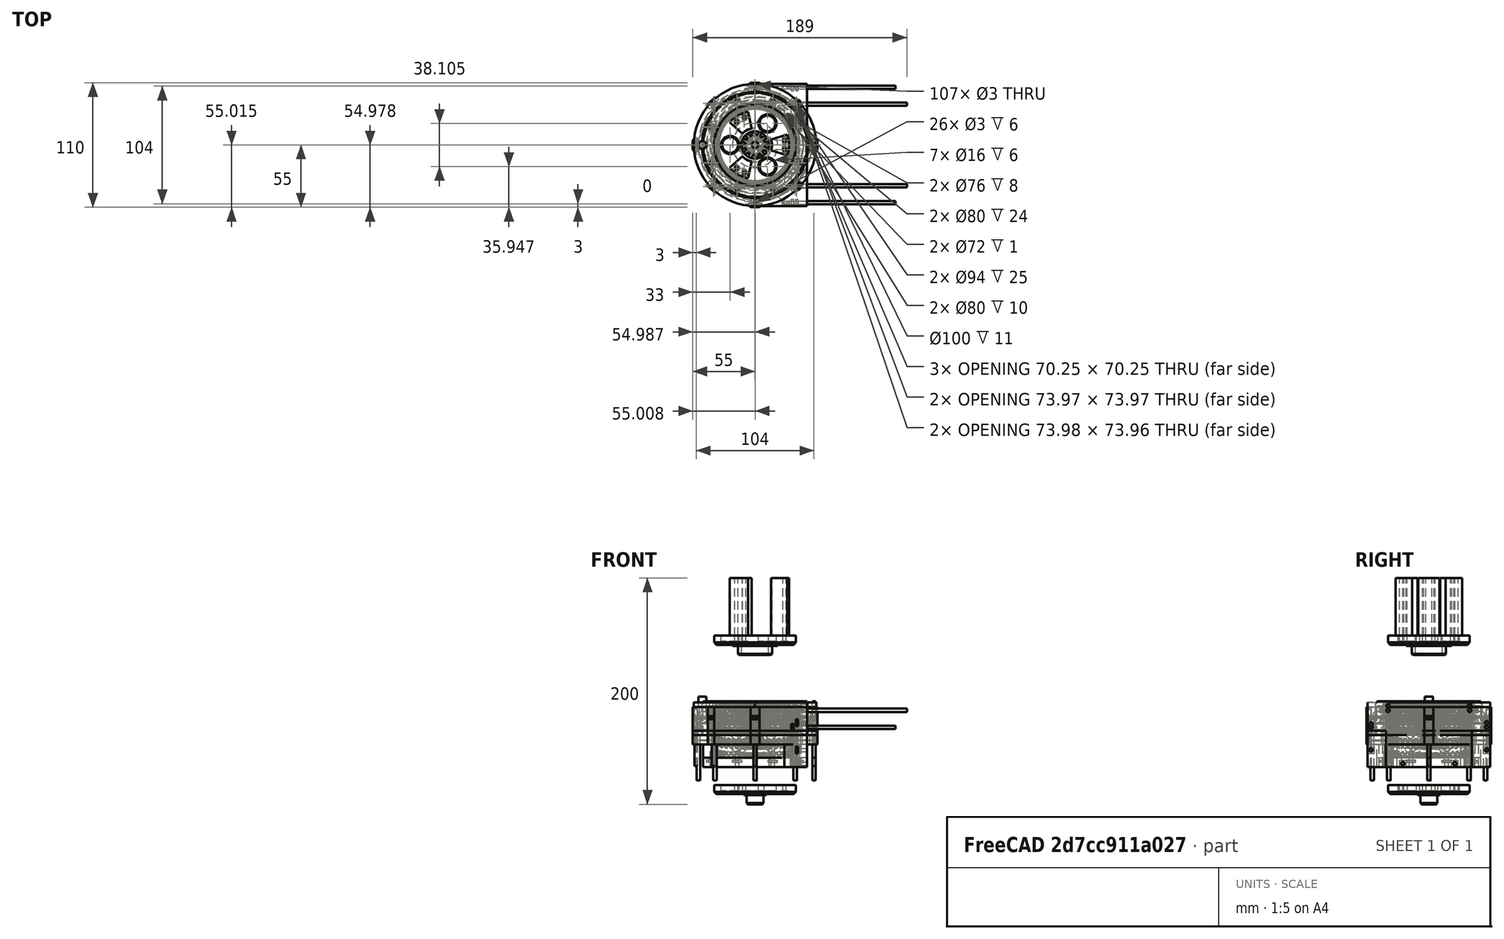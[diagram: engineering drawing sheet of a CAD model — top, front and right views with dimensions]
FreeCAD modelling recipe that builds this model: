
FCSTD DOCUMENT  (FreeCAD 0.19R24276 (Git))
Label: J-midi-deep-thin_039
License: All rights reserved
LicenseURL: http://en.wikipedia.org/wiki/All_rights_reserved
objects: Part::Cylinder×296, Part::Box×209, Part::Compound×127, Part::Cut×109, Part::FeaturePython×43, Part::Chamfer×31, Part::Torus×4, Part::Wedge×4, Mesh::Feature×3, Part::Mirroring×2, Part::Fillet×1
note: 826 computed .brp shape members not serialized (recipe doc carries the construction recipe); baked Part::Feature solids carry a one-line shape summary decoded from their .brp

FEATURE [Part::Torus] Torus004  label="Anuloid004"
  Angle1 = -180
  Angle2 = 180
  Angle3 = 360
  AttacherType = Attacher::AttachEngine3D
  Placement = pos=(0,0,34) rot=(0,0,1;0rad)
  Radius1 = 46.2
  Radius2 = 3.1
FEATURE [Part::Torus] Torus005  label="Anuloid005"
  Angle1 = -180
  Angle2 = 180
  Angle3 = 360
  AttacherType = Attacher::AttachEngine3D
  Placement = pos=(0,0,34) rot=(0,0,1;0rad)
  Radius1 = 46.2
  Radius2 = 3.1
FEATURE [Part::Box] Box157  label="Krychle157"
  AttacherType = Attacher::AttachEngine3D
  Height = 2
  Length = 8
  Placement = pos=(46,-3,23) rot=(0,0,1;0rad)
  Width = 6
FEATURE [Part::Cylinder] Cylinder006  label="Válec006"
  Angle = 360
  AttacherType = Attacher::AttachEngine3D
  Height = 16
  Placement = pos=(-45.6,0,34) rot=(0,0,1;0rad)
  Radius = 3.5
FEATURE [Part::Box] Box156  label="Krychle156"
  AttacherType = Attacher::AttachEngine3D
  Height = 25
  Length = 46
  Placement = pos=(0,-54,20) rot=(0,0,1;0rad)
  Width = 108
FEATURE [Part::Box] Box158  label="Krychle158"
  AttacherType = Attacher::AttachEngine3D
  Height = 2
  Length = 8
  Placement = pos=(34.6482,30.4056,23) rot=(0,0,1;0.785398rad)
  Width = 6
FEATURE [Part::Box] Box159  label="Krychle159"
  AttacherType = Attacher::AttachEngine3D
  Height = 2
  Length = 8
  Placement = pos=(3,46,23) rot=(0,0,1;1.5708rad)
  Width = 6
FEATURE [Part::Box] Box160  label="Krychle160"
  AttacherType = Attacher::AttachEngine3D
  Height = 2
  Length = 8
  Placement = pos=(-30.4056,34.6482,23) rot=(0,0,1;2.35619rad)
  Width = 6
FEATURE [Part::Box] Box161  label="Krychle161"
  AttacherType = Attacher::AttachEngine3D
  Height = 2
  Length = 8
  Placement = pos=(-46,3,23) rot=(0,0,1;3.14159rad)
  Width = 6
FEATURE [Part::Cylinder] Cylinder374  label="Válec374"
  Angle = 360
  AttacherType = Attacher::AttachEngine3D
  Height = 50
  Placement = pos=(50,0,-15) rot=(0,0,1;0rad)
  Radius = 1.5
FEATURE [Part::Cylinder] Cylinder375  label="Válec375"
  Angle = 360
  AttacherType = Attacher::AttachEngine3D
  Height = 50
  Placement = pos=(35.3553,35.3553,-15) rot=(0,0,1;0.785398rad)
  Radius = 1.5
FEATURE [Part::Cylinder] Cylinder376  label="Válec376"
  Angle = 360
  AttacherType = Attacher::AttachEngine3D
  Height = 50
  Placement = pos=(-7e-15,50,-15) rot=(0,0,1;1.5708rad)
  Radius = 1.5
FEATURE [Part::Box] Box162  label="Krychle162"
  AttacherType = Attacher::AttachEngine3D
  Height = 2
  Length = 8
  Placement = pos=(-34.6482,-30.4056,23) rot=(0,0,1;3.92699rad)
  Width = 6
FEATURE [Part::Box] Box163  label="Krychle163"
  AttacherType = Attacher::AttachEngine3D
  Height = 2
  Length = 8
  Placement = pos=(-3,-46,23) rot=(0,0,-1;1.5708rad)
  Width = 6
FEATURE [Part::Box] Box164  label="Krychle164"
  AttacherType = Attacher::AttachEngine3D
  Height = 2
  Length = 8
  Placement = pos=(30.4056,-34.6482,23) rot=(0,0,-1;0.785398rad)
  Width = 6
FEATURE [Part::Compound] Compound297
  Links = -> [Box157,Box158,Box159,Box160,Box161,Box162,Box163,Box164]
  Placement = pos=(0,0,1) rot=(0,0,1;0rad)
FEATURE [Part::Cylinder] Cylinder377  label="Válec377"
  Angle = 360
  AttacherType = Attacher::AttachEngine3D
  Height = 50
  Placement = pos=(-35.3553,35.3553,-15) rot=(0,0,1;2.35619rad)
  Radius = 1.5
FEATURE [Part::Cylinder] Cylinder378  label="Válec378"
  Angle = 360
  AttacherType = Attacher::AttachEngine3D
  Height = 50
  Placement = pos=(-50,-2.3e-14,-15) rot=(0,0,1;3.14159rad)
  Radius = 1.5
FEATURE [Part::Cylinder] Cylinder379  label="Válec379"
  Angle = 360
  AttacherType = Attacher::AttachEngine3D
  Height = 50
  Placement = pos=(-35.3553,-35.3553,-15) rot=(0,0,1;3.92699rad)
  Radius = 1.5
FEATURE [Part::Cylinder] Cylinder380  label="Válec380"
  Angle = 360
  AttacherType = Attacher::AttachEngine3D
  Height = 50
  Placement = pos=(2.5e-14,-50,-15) rot=(0,0,-1;1.5708rad)
  Radius = 1.5
FEATURE [Part::Cylinder] Cylinder381  label="Válec381"
  Angle = 360
  AttacherType = Attacher::AttachEngine3D
  Height = 50
  Placement = pos=(35.3553,-35.3553,-15) rot=(0,0,-1;0.785398rad)
  Radius = 1.5
FEATURE [Part::Compound] Compound298
  Links = -> [Cylinder374,Cylinder375,Cylinder376,Cylinder377,Cylinder378,Cylinder379,Cylinder380,Cylinder381]
  Placement = pos=(0,0,-5) rot=(0,0,1;0rad)
FEATURE [Part::Box] Box165  label="Krychle165"
  AttacherType = Attacher::AttachEngine3D
  Height = 2
  Length = 8
  Placement = pos=(3,46,23) rot=(0,0,1;1.5708rad)
  Width = 6
FEATURE [Part::Box] Box166  label="Krychle166"
  AttacherType = Attacher::AttachEngine3D
  Height = 2
  Length = 8
  Placement = pos=(-30.4056,34.6482,23) rot=(0,0,1;2.35619rad)
  Width = 6
FEATURE [Part::Box] Box167  label="Krychle167"
  AttacherType = Attacher::AttachEngine3D
  Height = 2
  Length = 8
  Placement = pos=(46,-3,23) rot=(0,0,1;0rad)
  Width = 6
FEATURE [Part::Box] Box168  label="Krychle168"
  AttacherType = Attacher::AttachEngine3D
  Height = 2
  Length = 8
  Placement = pos=(-46,3,23) rot=(0,0,1;3.14159rad)
  Width = 6
FEATURE [Part::Box] Box169  label="Krychle169"
  AttacherType = Attacher::AttachEngine3D
  Height = 2
  Length = 8
  Placement = pos=(-34.6482,-30.4056,23) rot=(0,0,1;3.92699rad)
  Width = 6
FEATURE [Part::Box] Box170  label="Krychle170"
  AttacherType = Attacher::AttachEngine3D
  Height = 2
  Length = 8
  Placement = pos=(30.4056,-34.6482,23) rot=(0,0,-1;0.785398rad)
  Width = 6
FEATURE [Part::Box] Box171  label="Krychle171"
  AttacherType = Attacher::AttachEngine3D
  Height = 2
  Length = 8
  Placement = pos=(34.6482,30.4056,23) rot=(0,0,1;0.785398rad)
  Width = 6
FEATURE [Part::Box] Box172  label="Krychle172"
  AttacherType = Attacher::AttachEngine3D
  Height = 2
  Length = 8
  Placement = pos=(-3,-46,23) rot=(0,0,-1;1.5708rad)
  Width = 6
FEATURE [Part::Compound] Compound300
  Links = -> [Box167,Box171,Box165,Box166,Box168,Box169,Box172,Box170]
  Placement = pos=(0,0,1) rot=(0,0,1;0rad)
FEATURE [Part::Cylinder] Cylinder  label="Válec"
  Angle = 360
  AttacherType = Attacher::AttachEngine3D
  Height = 25
  Placement = pos=(0,0,20) rot=(0,0,1;0rad)
  Radius = 47
FEATURE [Part::Cut] Cut153
  Base = -> Box156
  Tool = -> Cylinder
FEATURE [Part::Cut] Cut154
  Base = -> Cut153
  Tool = -> Torus005
FEATURE [Part::Cut] Cut155
  Base = -> Cut154
  Tool = -> Compound298
FEATURE [Part::Box] Box173  label="Krychle173"
  AttacherType = Attacher::AttachEngine3D
  Height = 6
  Length = 2
  Placement = pos=(32,48,24) rot=(0,0,1;0rad)
  Width = 6
FEATURE [Part::Cylinder] Cylinder391  label="Válec391"
  Angle = 360
  AttacherType = Attacher::AttachEngine3D
  Height = 100
  Placement = pos=(24,51,27) rot=(0,1,0;1.5708rad)
  Radius = 1.5
FEATURE [Part::Cylinder] Cylinder392  label="Válec392"
  Angle = 360
  AttacherType = Attacher::AttachEngine3D
  Height = 100
  Placement = pos=(24,-51,26) rot=(0,1,0;1.5708rad)
  Radius = 1.5
FEATURE [Part::Box] Box174  label="Krychle174"
  AttacherType = Attacher::AttachEngine3D
  Height = 6
  Length = 2
  Placement = pos=(32,-54,24) rot=(0,0,1;0rad)
  Width = 6
FEATURE [Part::Box] Box175  label="Krychle175"
  AttacherType = Attacher::AttachEngine3D
  Height = 6
  Length = 2
  Placement = pos=(38,33,39) rot=(0,0,1;0rad)
  Width = 6
FEATURE [Part::Cylinder] Cylinder393  label="Válec393"
  Angle = 360
  AttacherType = Attacher::AttachEngine3D
  Height = 100
  Placement = pos=(34,36,42) rot=(0,1,0;1.5708rad)
  Radius = 1.5
FEATURE [Part::Cylinder] Cylinder394  label="Válec394"
  Angle = 360
  AttacherType = Attacher::AttachEngine3D
  Height = 100
  Placement = pos=(34,-36,42) rot=(0,1,0;1.5708rad)
  Radius = 1.5
FEATURE [Part::Compound] Compound301
  Links = -> [Cylinder391,Cylinder392,Cylinder393,Cylinder394]
FEATURE [Part::Box] Box176  label="Krychle176"
  AttacherType = Attacher::AttachEngine3D
  Height = 6
  Length = 2
  Placement = pos=(38,-39,39) rot=(0,0,1;0rad)
  Width = 6
FEATURE [Part::Compound] Compound302
  Links = -> [Box173,Box174,Box175,Box176]
FEATURE [Part::Cylinder] Cylinder395  label="Válec395"
  Angle = 360
  AttacherType = Attacher::AttachEngine3D
  Height = 100
  Placement = pos=(34,-36,42) rot=(0,1,0;1.5708rad)
  Radius = 1.5
FEATURE [Part::Cylinder] Cylinder396  label="Válec396"
  Angle = 360
  AttacherType = Attacher::AttachEngine3D
  Height = 100
  Placement = pos=(24,51,27) rot=(0,1,0;1.5708rad)
  Radius = 1.5
FEATURE [Part::Cylinder] Cylinder397  label="Válec397"
  Angle = 360
  AttacherType = Attacher::AttachEngine3D
  Height = 100
  Placement = pos=(24,-51,27) rot=(0,1,0;1.5708rad)
  Radius = 1.5
FEATURE [Part::Cylinder] Cylinder398  label="Válec398"
  Angle = 360
  AttacherType = Attacher::AttachEngine3D
  Height = 100
  Placement = pos=(34,36,42) rot=(0,1,0;1.5708rad)
  Radius = 1.5
FEATURE [Part::Compound] Compound303
  Links = -> [Cylinder396,Cylinder397,Cylinder398,Cylinder395]
FEATURE [Part::Box] Box177  label="Krychle177"
  AttacherType = Attacher::AttachEngine3D
  Height = 6
  Length = 2
  Placement = pos=(36,48,24) rot=(0,0,1;0rad)
  Width = 6
FEATURE [Part::Box] Box178  label="Krychle178"
  AttacherType = Attacher::AttachEngine3D
  Height = 6
  Length = 2
  Placement = pos=(36,-54,24) rot=(0,0,1;0rad)
  Width = 6
FEATURE [Part::Box] Box179  label="Krychle179"
  AttacherType = Attacher::AttachEngine3D
  Height = 6
  Length = 2
  Placement = pos=(38,33,39) rot=(0,0,1;0rad)
  Width = 6
FEATURE [Part::Box] Box180  label="Krychle180"
  AttacherType = Attacher::AttachEngine3D
  Height = 6
  Length = 2
  Placement = pos=(38,-39,39) rot=(0,0,1;0rad)
  Width = 6
FEATURE [Part::Compound] Compound304
  Links = -> [Box177,Box178,Box179,Box180]
FEATURE [Part::FeaturePython] Tube002  # WARN: FeaturePython — macro-defined, semantics opaque (R4)
  AttacherType = Attacher::AttachEngine3D
  Height = 25
  InnerRadius = 47
  OuterRadius = 54
  Placement = pos=(0,0,20) rot=(0,0,1;0rad)
FEATURE [Part::Cut] Cut156
  Base = -> Cut155
  Tool = -> Compound300
FEATURE [Part::Cut] Cut157
  Base = -> Cut156
  Tool = -> Compound301
FEATURE [Part::Cut] Cut158
  Base = -> Cut157
  Tool = -> Compound304
FEATURE [Part::Cut] Cut009
  Base = -> Tube002
  Tool = -> Torus004
FEATURE [Part::Cut] Cut010
  Base = -> Cut009
  Tool = -> Cylinder006
FEATURE [Part::Cut] Cut151
  Base = -> Cut010
  Tool = -> Compound297
FEATURE [Part::Cut] Cut152
  Base = -> Cut151
  Tool = -> Compound298
FEATURE [Part::Cut] Cut159
  Base = -> Cut152
  Tool = -> Compound303
FEATURE [Part::Cut] Cut160
  Base = -> Cut159
  Tool = -> Compound302
FEATURE [Part::Compound] Compound728  label="J-midi-deep_bearing-ring"
  Links = -> [Cut160,Cut158]
  Placement = pos=(0,0,4) rot=(0,0,1;0rad)
FEATURE [Part::Torus] Torus009  label="Anuloid009"
  Angle1 = -180
  Angle2 = 180
  Angle3 = 360
  AttacherType = Attacher::AttachEngine3D
  Placement = pos=(0,0,34) rot=(0,0,1;0rad)
  Radius1 = 46
  Radius2 = 3.1
FEATURE [Part::Box] Box424  label="Krychle424"
  AttacherType = Attacher::AttachEngine3D
  Height = 2
  Length = 6
  Placement = pos=(30.4056,-34.6482,33) rot=(0,0,1;0.785398rad)
  Width = 8
FEATURE [Part::Cylinder] Cylinder1114  label="Válec1114"
  Angle = 360
  AttacherType = Attacher::AttachEngine3D
  Height = 20
  Placement = pos=(-46.4,0,34) rot=(0,0,1;0rad)
  Radius = 3.5
FEATURE [Part::Box] Box425  label="Krychle425"
  AttacherType = Attacher::AttachEngine3D
  Height = 2
  Length = 6
  Placement = pos=(3,46,33) rot=(0,0,1;3.14159rad)
  Width = 8
FEATURE [Part::Box] Box426  label="Krychle426"
  AttacherType = Attacher::AttachEngine3D
  Height = 2
  Length = 6
  Placement = pos=(-3,-46,33) rot=(0,0,1;0rad)
  Width = 8
FEATURE [Part::Cylinder] Cylinder1115  label="Válec1115"
  Angle = 360
  AttacherType = Attacher::AttachEngine3D
  Height = 12
  Radius = 40
FEATURE [Part::Cylinder] Cylinder1116  label="Válec1116"
  Angle = 360
  AttacherType = Attacher::AttachEngine3D
  Height = 12
  Radius = 40
FEATURE [Part::Box] Box427  label="Krychle427"
  AttacherType = Attacher::AttachEngine3D
  Height = 2
  Length = 6
  Placement = pos=(-46,3,33) rot=(0,0,-1;1.5708rad)
  Width = 8
FEATURE [Part::Box] Box428  label="Krychle428"
  AttacherType = Attacher::AttachEngine3D
  Height = 2
  Length = 6
  Placement = pos=(-3,-46,33) rot=(0,0,1;0rad)
  Width = 8
FEATURE [Part::Box] Box429  label="Krychle429"
  AttacherType = Attacher::AttachEngine3D
  Height = 2
  Length = 6
  Placement = pos=(-46,3,33) rot=(0,0,-1;1.5708rad)
  Width = 8
FEATURE [Part::Box] Box430  label="Krychle430"
  AttacherType = Attacher::AttachEngine3D
  Height = 2
  Length = 6
  Placement = pos=(-34.6482,-30.4056,33) rot=(0,0,-1;0.785398rad)
  Width = 8
FEATURE [Part::Box] Box431  label="Krychle431"
  AttacherType = Attacher::AttachEngine3D
  Height = 2
  Length = 6
  Placement = pos=(46,-3,33) rot=(0,0,1;1.5708rad)
  Width = 8
FEATURE [Part::Box] Box432  label="Krychle432"
  AttacherType = Attacher::AttachEngine3D
  Height = 2
  Length = 6
  Placement = pos=(34.6482,30.4056,33) rot=(0,0,1;2.35619rad)
  Width = 8
FEATURE [Part::Box] Box433  label="Krychle433"
  AttacherType = Attacher::AttachEngine3D
  Height = 2
  Length = 6
  Placement = pos=(30.4056,-34.6482,33) rot=(0,0,1;0.785398rad)
  Width = 8
FEATURE [Part::Box] Box434  label="Krychle434"
  AttacherType = Attacher::AttachEngine3D
  Height = 2
  Length = 6
  Placement = pos=(-30.4056,34.6482,33) rot=(0,0,1;3.92699rad)
  Width = 8
FEATURE [Part::Compound] Compound870
  Links = -> [Box430,Box424,Box431,Box428,Box432,Box425,Box434,Box427]
  Placement = pos=(0,0,7) rot=(0,0,1;0.392699rad)
FEATURE [Part::Box] Box435  label="Krychle435"
  AttacherType = Attacher::AttachEngine3D
  Height = 2
  Length = 6
  Placement = pos=(46,-3,33) rot=(0,0,1;1.5708rad)
  Width = 8
FEATURE [Part::Box] Box436  label="Krychle436"
  AttacherType = Attacher::AttachEngine3D
  Height = 2
  Length = 6
  Placement = pos=(3,46,33) rot=(0,0,1;3.14159rad)
  Width = 8
FEATURE [Part::Cylinder] Cylinder1117  label="Válec1117"
  Angle = 360
  AttacherType = Attacher::AttachEngine3D
  Height = 20
  Placement = pos=(-46.4,0,34) rot=(0,0,1;0rad)
  Radius = 3.5
FEATURE [Part::Cylinder] Cylinder1118  label="Válec1118"
  Angle = 360
  AttacherType = Attacher::AttachEngine3D
  Height = 32
  Placement = pos=(-29.6985,-29.6985,33.5) rot=(0,0,-1;0.785398rad)
  Radius = 1.5
FEATURE [Part::Cylinder] Cylinder1119  label="Válec1119"
  Angle = 360
  AttacherType = Attacher::AttachEngine3D
  Height = 12
  Placement = pos=(-29.6985,-29.6985,33.5) rot=(0,0,-1;0.785398rad)
  Radius = 1.5
FEATURE [Part::Cylinder] Cylinder1120  label="Válec1120"
  Angle = 360
  AttacherType = Attacher::AttachEngine3D
  Height = 12
  Placement = pos=(29.6985,-29.6985,33.5) rot=(0,0,1;0.785398rad)
  Radius = 1.5
FEATURE [Part::Box] Box437  label="Krychle437"
  AttacherType = Attacher::AttachEngine3D
  Height = 2
  Length = 6
  Placement = pos=(-34.6482,-30.4056,33) rot=(0,0,-1;0.785398rad)
  Width = 8
FEATURE [Part::Cylinder] Cylinder1121  label="Válec1121"
  Angle = 360
  AttacherType = Attacher::AttachEngine3D
  Height = 32
  Placement = pos=(0,-42,33.5) rot=(0,0,1;0rad)
  Radius = 1.5
FEATURE [Part::Cylinder] Cylinder1122  label="Válec1122"
  Angle = 360
  AttacherType = Attacher::AttachEngine3D
  Height = 12
  Placement = pos=(0,-42,33.5) rot=(0,0,1;0rad)
  Radius = 1.5
FEATURE [Part::Cylinder] Cylinder1123  label="Válec1123"
  Angle = 360
  AttacherType = Attacher::AttachEngine3D
  Height = 32
  Placement = pos=(-1.4e-14,42,33.5) rot=(0,0,1;3.14159rad)
  Radius = 1.5
FEATURE [Part::Cylinder] Cylinder1124  label="Válec1124"
  Angle = 360
  AttacherType = Attacher::AttachEngine3D
  Height = 12
  Placement = pos=(-42,-2.4e-14,33.5) rot=(0,0,-1;1.5708rad)
  Radius = 1.5
FEATURE [Part::Cylinder] Cylinder1125  label="Válec1125"
  Angle = 360
  AttacherType = Attacher::AttachEngine3D
  Height = 12
  Placement = pos=(-1.4e-14,42,33.5) rot=(0,0,1;3.14159rad)
  Radius = 1.5
FEATURE [Part::Box] Box438  label="Krychle438"
  AttacherType = Attacher::AttachEngine3D
  Height = 2
  Length = 6
  Placement = pos=(34.6482,30.4056,33) rot=(0,0,1;2.35619rad)
  Width = 8
FEATURE [Part::Cylinder] Cylinder1126  label="Válec1126"
  Angle = 360
  AttacherType = Attacher::AttachEngine3D
  Height = 12
  Placement = pos=(29.6985,29.6985,33.5) rot=(0,0,1;2.35619rad)
  Radius = 1.5
FEATURE [Part::Box] Box439  label="Krychle439"
  AttacherType = Attacher::AttachEngine3D
  Height = 2
  Length = 6
  Placement = pos=(-34.6482,-30.4056,33) rot=(0,0,-1;0.785398rad)
  Width = 8
FEATURE [Part::Box] Box440  label="Krychle440"
  AttacherType = Attacher::AttachEngine3D
  Height = 2
  Length = 6
  Placement = pos=(-30.4056,34.6482,33) rot=(0,0,1;3.92699rad)
  Width = 8
FEATURE [Part::Compound] Compound873
  Links = -> [Box439,Box433,Box435,Box426,Box438,Box436,Box440,Box429]
  Placement = pos=(0,0,7) rot=(0,0,1;0.392699rad)
FEATURE [Part::Cylinder] Cylinder1127  label="Válec1127"
  Angle = 360
  AttacherType = Attacher::AttachEngine3D
  Height = 12
  Placement = pos=(-29.6985,29.6985,33.5) rot=(0,0,1;3.92699rad)
  Radius = 1.5
FEATURE [Part::Cylinder] Cylinder1128  label="Válec1128"
  Angle = 360
  AttacherType = Attacher::AttachEngine3D
  Height = 12
  Placement = pos=(42,6e-15,33.5) rot=(0,0,1;1.5708rad)
  Radius = 1.5
FEATURE [Part::Compound] Compound874
  Links = -> [Cylinder1122,Cylinder1120,Cylinder1128,Cylinder1126,Cylinder1125,Cylinder1127,Cylinder1124,Cylinder1119]
  Placement = pos=(0,0,4) rot=(0,0,1;0.392699rad)
FEATURE [Part::Box] Box441  label="Krychle441"
  AttacherType = Attacher::AttachEngine3D
  Height = 2
  Length = 6
  Placement = pos=(-30.4056,34.6482,33) rot=(0,0,1;3.92699rad)
  Width = 8
FEATURE [Part::Box] Box442  label="Krychle442"
  AttacherType = Attacher::AttachEngine3D
  Height = 2
  Length = 6
  Placement = pos=(-3,-46,33) rot=(0,0,1;0rad)
  Width = 8
FEATURE [Part::Box] Box443  label="Krychle443"
  AttacherType = Attacher::AttachEngine3D
  Height = 2
  Length = 6
  Placement = pos=(46,-3,33) rot=(0,0,1;1.5708rad)
  Width = 8
FEATURE [Part::Cylinder] Cylinder1129  label="Válec1129"
  Angle = 360
  AttacherType = Attacher::AttachEngine3D
  Height = 32
  Placement = pos=(-29.6985,29.6985,33.5) rot=(0,0,1;3.92699rad)
  Radius = 1.5
FEATURE [Part::Box] Box444  label="Krychle444"
  AttacherType = Attacher::AttachEngine3D
  Height = 2
  Length = 6
  Placement = pos=(-46,3,33) rot=(0,0,-1;1.5708rad)
  Width = 8
FEATURE [Part::Box] Box445  label="Krychle445"
  AttacherType = Attacher::AttachEngine3D
  Height = 2
  Length = 6
  Placement = pos=(30.4056,-34.6482,33) rot=(0,0,1;0.785398rad)
  Width = 8
FEATURE [Part::Cylinder] Cylinder1130  label="Válec1130"
  Angle = 360
  AttacherType = Attacher::AttachEngine3D
  Height = 32
  Placement = pos=(-42,-2.4e-14,33.5) rot=(0,0,-1;1.5708rad)
  Radius = 1.5
FEATURE [Part::Box] Box446  label="Krychle446"
  AttacherType = Attacher::AttachEngine3D
  Height = 2
  Length = 6
  Placement = pos=(3,46,33) rot=(0,0,1;3.14159rad)
  Width = 8
FEATURE [Part::Cylinder] Cylinder1131  label="Válec1131"
  Angle = 360
  AttacherType = Attacher::AttachEngine3D
  Height = 32
  Placement = pos=(29.6985,29.6985,33.5) rot=(0,0,1;2.35619rad)
  Radius = 1.5
FEATURE [Part::Box] Box447  label="Krychle447"
  AttacherType = Attacher::AttachEngine3D
  Height = 2
  Length = 6
  Placement = pos=(34.6482,30.4056,33) rot=(0,0,1;2.35619rad)
  Width = 8
FEATURE [Part::Compound] Compound869
  Links = -> [Box437,Box445,Box443,Box442,Box447,Box446,Box441,Box444]
  Placement = pos=(0,0,7) rot=(0,0,1;0.392699rad)
FEATURE [Part::Cylinder] Cylinder1132  label="Válec1132"
  Angle = 360
  AttacherType = Attacher::AttachEngine3D
  Height = 32
  Placement = pos=(42,6e-15,33.5) rot=(0,0,1;1.5708rad)
  Radius = 1.5
FEATURE [Part::Cylinder] Cylinder1133  label="Válec1133"
  Angle = 360
  AttacherType = Attacher::AttachEngine3D
  Height = 32
  Placement = pos=(29.6985,-29.6985,33.5) rot=(0,0,1;0.785398rad)
  Radius = 1.5
FEATURE [Part::Compound] Compound871
  Links = -> [Cylinder1121,Cylinder1133,Cylinder1132,Cylinder1131,Cylinder1123,Cylinder1129,Cylinder1130,Cylinder1118]
  Placement = pos=(0,0,4) rot=(0,0,1;0.392699rad)
FEATURE [Part::FeaturePython] wormgear065  # WARN: FeaturePython — macro-defined, semantics opaque (R4)
  AttacherType = Attacher::AttachEngine3D
  Placement = pos=(0,0,0) rot=(0,0,-1;0.1309rad)
  beta = 38.7636
  clearance = 0.25
  diameter = 67.25
  head = 0
  height = 14
  module = 1.5
  pressure_angle = 20
  reverse_pitch = false
  teeth = 36
  version = 0.0.3
FEATURE [Part::Cut] Cut418
  Base = -> Cylinder1116
  Placement = pos=(0,0,21) rot=(0,0,1;0.258309rad)
  Tool = -> wormgear065
FEATURE [Part::FeaturePython] Tube100  # WARN: FeaturePython — macro-defined, semantics opaque (R4)
  AttacherType = Attacher::AttachEngine3D
  Height = 24
  InnerRadius = 40
  OuterRadius = 46
  Placement = pos=(0,0,21) rot=(0,0,1;0rad)
FEATURE [Part::Cut] Cut419
  Base = -> Tube100
  Tool = -> Torus009
FEATURE [Part::Cut] Cut426
  Base = -> Cut419
  Tool = -> Cylinder1114
FEATURE [Part::Cut] Cut420
  Base = -> Cut426
  Tool = -> Compound871
FEATURE [Part::Cut] Cut421
  Base = -> Cut420
  Tool = -> Compound869
FEATURE [Part::FeaturePython] wormgear066  # WARN: FeaturePython — macro-defined, semantics opaque (R4)
  AttacherType = Attacher::AttachEngine3D
  Placement = pos=(0,0,0) rot=(0,0,1;0.10472rad)
  beta = 38.7636
  clearance = 0.25
  diameter = 67.25
  head = 0
  height = 14
  module = 1.5
  pressure_angle = 20
  reverse_pitch = true
  teeth = 36
  version = 0.0.3
FEATURE [Part::Cut] Cut423
  Base = -> Cylinder1115
  Placement = pos=(0,0,33) rot=(0,0,1;0.466876rad)
  Tool = -> wormgear066
FEATURE [Part::Cut] Cut427
  Base = -> Cut423
  Tool = -> Compound870
FEATURE [Part::Compound] Compound872
  Links = -> [Cut427,Cut418]
FEATURE [Part::FeaturePython] Tube101  # WARN: FeaturePython — macro-defined, semantics opaque (R4)
  AttacherType = Attacher::AttachEngine3D
  Height = 1
  InnerRadius = 36
  OuterRadius = 46
  Placement = pos=(0,0,45) rot=(0,0,1;0rad)
FEATURE [Part::Cut] Cut424
  Base = -> Tube101
  Tool = -> Cylinder1117
FEATURE [Part::Cut] Cut425
  Base = -> Cut424
  Tool = -> Compound874
FEATURE [Part::Cut] Cut422
  Base = -> Cut425
  Tool = -> Compound873
FEATURE [Part::Compound] Compound875  label="J-midi_actuator-ring-m1.5_v4"
  Links = -> [Cut421,Cut422,Compound872]
FEATURE [Part::FeaturePython] Tube102  # WARN: FeaturePython — macro-defined, semantics opaque (R4)
  AttacherType = Attacher::AttachEngine3D
  Height = 25
  InnerRadius = 47
  OuterRadius = 54
  Placement = pos=(0,0,20) rot=(0,0,1;0rad)
FEATURE [Part::FeaturePython] Tube103  # WARN: FeaturePython — macro-defined, semantics opaque (R4)
  AttacherType = Attacher::AttachEngine3D
  Height = 24
  InnerRadius = 40
  OuterRadius = 46
  Placement = pos=(0,0,21) rot=(0,0,1;0rad)
FEATURE [Part::FeaturePython] Tube  label="61816"  # WARN: FeaturePython — macro-defined, semantics opaque (R4)
  AttacherType = Attacher::AttachEngine3D
  Height = 10
  InnerRadius = 40
  OuterRadius = 50
  Placement = pos=(0,0,20) rot=(0,0,1;0rad)
FEATURE [Part::Cylinder] Cylinder1134  label="Válec1134"
  Angle = 360
  AttacherType = Attacher::AttachEngine3D
  Height = 50
  Placement = pos=(52,0,-15) rot=(0,0,1;0rad)
  Radius = 1.5
FEATURE [Part::Cylinder] Cylinder1135  label="Válec1135"
  Angle = 360
  AttacherType = Attacher::AttachEngine3D
  Height = 50
  Placement = pos=(35.3553,35.3553,-15) rot=(0,0,1;0.785398rad)
  Radius = 1.5
FEATURE [Part::Cylinder] Cylinder1136  label="Válec1136"
  Angle = 360
  AttacherType = Attacher::AttachEngine3D
  Height = 50
  Placement = pos=(-7e-15,50,-15) rot=(0,0,1;1.5708rad)
  Radius = 1.5
FEATURE [Part::Cylinder] Cylinder1137  label="Válec1137"
  Angle = 360
  AttacherType = Attacher::AttachEngine3D
  Height = 50
  Placement = pos=(-35.3553,35.3553,-15) rot=(0,0,1;2.35619rad)
  Radius = 1.5
FEATURE [Part::Cylinder] Cylinder1138  label="Válec1138"
  Angle = 360
  AttacherType = Attacher::AttachEngine3D
  Height = 50
  Placement = pos=(-50,-2.3e-14,-15) rot=(0,0,1;3.14159rad)
  Radius = 1.5
FEATURE [Part::Cylinder] Cylinder1139  label="Válec1139"
  Angle = 360
  AttacherType = Attacher::AttachEngine3D
  Height = 50
  Placement = pos=(-35.3553,-35.3553,-15) rot=(0,0,1;3.92699rad)
  Radius = 1.5
FEATURE [Part::Cylinder] Cylinder1140  label="Válec1140"
  Angle = 360
  AttacherType = Attacher::AttachEngine3D
  Height = 50
  Placement = pos=(2.5e-14,-50,-15) rot=(0,0,-1;1.5708rad)
  Radius = 1.5
FEATURE [Part::Cylinder] Cylinder1141  label="Válec1141"
  Angle = 360
  AttacherType = Attacher::AttachEngine3D
  Height = 50
  Placement = pos=(35.3553,-35.3553,-15) rot=(0,0,-1;0.785398rad)
  Radius = 1.5
FEATURE [Part::Compound] Compound876
  Links = -> [Cylinder1134,Cylinder1135,Cylinder1136,Cylinder1137,Cylinder1138,Cylinder1139,Cylinder1140,Cylinder1141]
  Placement = pos=(0,0,-5) rot=(0,0,1;0rad)
FEATURE [Part::Cylinder] Cylinder1142  label="Válec1142"
  Angle = 360
  AttacherType = Attacher::AttachEngine3D
  Height = 50
  Placement = pos=(52,0,0) rot=(0,0,1;0rad)
  Radius = 1.5
FEATURE [Part::Cut] Cut  label="Thino"
  Base = -> Tube102
  Tool = -> Cylinder1142
FEATURE [Part::Box] Box448  label="Krychle448"
  AttacherType = Attacher::AttachEngine3D
  Height = 2
  Length = 8
  Placement = pos=(3,46,23) rot=(0,0,1;1.5708rad)
  Width = 6
FEATURE [Part::Box] Box449  label="Krychle449"
  AttacherType = Attacher::AttachEngine3D
  Height = 2
  Length = 8
  Placement = pos=(-30.4056,34.6482,23) rot=(0,0,1;2.35619rad)
  Width = 6
FEATURE [Part::Box] Box450  label="Krychle450"
  AttacherType = Attacher::AttachEngine3D
  Height = 2
  Length = 8
  Placement = pos=(46,-3,23) rot=(0,0,1;0rad)
  Width = 6
FEATURE [Part::Box] Box451  label="Krychle451"
  AttacherType = Attacher::AttachEngine3D
  Height = 2
  Length = 8
  Placement = pos=(-46,3,23) rot=(0,0,1;3.14159rad)
  Width = 6
FEATURE [Part::Box] Box452  label="Krychle452"
  AttacherType = Attacher::AttachEngine3D
  Height = 2
  Length = 8
  Placement = pos=(-34.6482,-30.4056,23) rot=(0,0,1;3.92699rad)
  Width = 6
FEATURE [Part::Box] Box453  label="Krychle453"
  AttacherType = Attacher::AttachEngine3D
  Height = 2
  Length = 8
  Placement = pos=(30.4056,-34.6482,23) rot=(0,0,-1;0.785398rad)
  Width = 6
FEATURE [Part::Box] Box454  label="Krychle454"
  AttacherType = Attacher::AttachEngine3D
  Height = 2
  Length = 8
  Placement = pos=(34.6482,30.4056,23) rot=(0,0,1;0.785398rad)
  Width = 6
FEATURE [Part::Box] Box455  label="Krychle455"
  AttacherType = Attacher::AttachEngine3D
  Height = 2
  Length = 8
  Placement = pos=(-3,-46,23) rot=(0,0,-1;1.5708rad)
  Width = 6
FEATURE [Part::Compound] Compound877
  Links = -> [Box450,Box454,Box448,Box449,Box451,Box452,Box455,Box453]
  Placement = pos=(0,0,1) rot=(0,0,1;0rad)
FEATURE [Part::Box] Box456  label="Krychle456"
  AttacherType = Attacher::AttachEngine3D
  Height = 2
  Length = 8
  Placement = pos=(47,-3,34) rot=(0,0,1;0rad)
  Width = 6
FEATURE [Part::FeaturePython] Tube104  # WARN: FeaturePython — macro-defined, semantics opaque (R4)
  AttacherType = Attacher::AttachEngine3D
  Height = 25
  InnerRadius = 47
  OuterRadius = 54
  Placement = pos=(0,0,20) rot=(0,0,1;0rad)
FEATURE [Part::Cylinder] Cylinder1143  label="Válec1143"
  Angle = 360
  AttacherType = Attacher::AttachEngine3D
  Height = 50
  Placement = pos=(52,0,0) rot=(0,0,1;0rad)
  Radius = 1.5
FEATURE [Part::Box] Box457  label="Krychle457"
  AttacherType = Attacher::AttachEngine3D
  Height = 25
  Length = 4
  Placement = pos=(51,-6,20) rot=(0,0,1;0rad)
  Width = 12
FEATURE [Part::Chamfer] Chamfer
  Base = -> Box457
  Edges = 2 edges r=2: [Edge5,Edge7]
FEATURE [Part::Cylinder] Cylinder1144  label="Válec1144"
  Angle = 360
  AttacherType = Attacher::AttachEngine3D
  Height = 50
  Placement = pos=(52,0,0) rot=(0,0,1;0rad)
  Radius = 1.5
FEATURE [Part::Cylinder] Cylinder1145  label="Válec1145"
  Angle = 360
  AttacherType = Attacher::AttachEngine3D
  Height = 50
  Placement = pos=(52,0,0) rot=(0,0,1;0rad)
  Radius = 1.5
FEATURE [Part::Cut] Cut428
  Base = -> Chamfer
  Tool = -> Cylinder1144
FEATURE [Part::Compound] Compound  label="J-midi_thin-ring_old"
  Links = -> [Cut,Cut428]
FEATURE [Part::FeaturePython] Tube105  label="ZKL-61816"  # WARN: FeaturePython — macro-defined, semantics opaque (R4)
  AttacherType = Attacher::AttachEngine3D
  Height = 10
  InnerRadius = 40
  OuterRadius = 50
  Placement = pos=(0,0,20) rot=(0,0,1;0rad)
FEATURE [Part::FeaturePython] Tube106  label="ZKL-61816-2"  # WARN: FeaturePython — macro-defined, semantics opaque (R4)
  AttacherType = Attacher::AttachEngine3D
  Height = 10
  InnerRadius = 40
  OuterRadius = 50
  Placement = pos=(0,0,20) rot=(0,0,1;0rad)
FEATURE [Part::FeaturePython] Tube107  # WARN: FeaturePython — macro-defined, semantics opaque (R4)
  AttacherType = Attacher::AttachEngine3D
  Height = 25
  InnerRadius = 47
  OuterRadius = 54
  Placement = pos=(0,0,20) rot=(0,0,1;0rad)
FEATURE [Part::Box] Box458  label="Krychle458"
  AttacherType = Attacher::AttachEngine3D
  Height = 25
  Length = 4
  Placement = pos=(51,-6,20) rot=(0,0,1;0rad)
  Width = 12
FEATURE [Part::Chamfer] Chamfer001
  Base = -> Box458
  Edges = 2 edges r=2: [Edge5,Edge7]
FEATURE [Part::Chamfer] Chamfer002
  Base = -> Box458
  Edges = 2 edges r=2: [Edge5,Edge7]
  Placement = pos=(0,0,0) rot=(0,0,1;0.785398rad)
FEATURE [Part::Chamfer] Chamfer003
  Base = -> Box458
  Edges = 2 edges r=2: [Edge5,Edge7]
  Placement = pos=(0,0,0) rot=(0,0,1;1.5708rad)
FEATURE [Part::Chamfer] Chamfer004
  Base = -> Box458
  Edges = 2 edges r=2: [Edge5,Edge7]
  Placement = pos=(0,0,0) rot=(0,0,1;2.35619rad)
FEATURE [Part::FeaturePython] Tube108  label="ZKL-61816-3"  # WARN: FeaturePython — macro-defined, semantics opaque (R4)
  AttacherType = Attacher::AttachEngine3D
  Height = 10
  InnerRadius = 40
  OuterRadius = 50
  Placement = pos=(0,0,25) rot=(0,0,1;0rad)
FEATURE [Part::FeaturePython] Tube109  label="ZKL-61816-003"  # WARN: FeaturePython — macro-defined, semantics opaque (R4)
  AttacherType = Attacher::AttachEngine3D
  Height = 11
  InnerRadius = 40
  OuterRadius = 50
  Placement = pos=(0,0,20) rot=(0,0,1;0rad)
FEATURE [Part::Chamfer] Chamfer005
  Base = -> Box458
  Edges = 2 edges r=2: [Edge5,Edge7]
  Placement = pos=(0,0,0) rot=(0,0,1;3.14159rad)
FEATURE [Part::Chamfer] Chamfer006
  Base = -> Box458
  Edges = 2 edges r=2: [Edge5,Edge7]
  Placement = pos=(0,0,0) rot=(0,0,1;3.92699rad)
FEATURE [Part::Chamfer] Chamfer007
  Base = -> Box458
  Edges = 2 edges r=2: [Edge5,Edge7]
  Placement = pos=(0,0,0) rot=(0,0,-1;1.5708rad)
FEATURE [Part::Chamfer] Chamfer008
  Base = -> Box458
  Edges = 2 edges r=2: [Edge5,Edge7]
  Placement = pos=(0,0,0) rot=(0,0,-1;0.785398rad)
FEATURE [Part::Compound] Compound878
  Links = -> [Chamfer001,Chamfer002,Chamfer003,Chamfer004,Chamfer005,Chamfer006,Chamfer007,Chamfer008]
FEATURE [Part::Cut] Cut429
  Base = -> Tube107
  Tool = -> Tube109
FEATURE [Part::Cylinder] Cylinder1152  label="Válec1152"
  Angle = 360
  AttacherType = Attacher::AttachEngine3D
  Height = 50
  Placement = pos=(52,0,0) rot=(0,0,1;0rad)
  Radius = 1.5
FEATURE [Part::Cylinder] Cylinder1153  label="Válec1153"
  Angle = 360
  AttacherType = Attacher::AttachEngine3D
  Height = 50
  Placement = pos=(36.7696,36.7696,0) rot=(0,0,1;0.785398rad)
  Radius = 1.5
FEATURE [Part::Cylinder] Cylinder1154  label="Válec1154"
  Angle = 360
  AttacherType = Attacher::AttachEngine3D
  Height = 50
  Placement = pos=(-7e-15,52,0) rot=(0,0,1;1.5708rad)
  Radius = 1.5
FEATURE [Part::Cylinder] Cylinder1155  label="Válec1155"
  Angle = 360
  AttacherType = Attacher::AttachEngine3D
  Height = 50
  Placement = pos=(-36.7696,36.7696,0) rot=(0,0,1;2.35619rad)
  Radius = 1.5
FEATURE [Part::Cylinder] Cylinder1156  label="Válec1156"
  Angle = 360
  AttacherType = Attacher::AttachEngine3D
  Height = 50
  Placement = pos=(-52,-2.1e-14,0) rot=(0,0,1;3.14159rad)
  Radius = 1.5
FEATURE [Part::Cylinder] Cylinder1157  label="Válec1157"
  Angle = 360
  AttacherType = Attacher::AttachEngine3D
  Height = 50
  Placement = pos=(-36.7696,-36.7696,0) rot=(0,0,1;3.92699rad)
  Radius = 1.5
FEATURE [Part::Cylinder] Cylinder1158  label="Válec1158"
  Angle = 360
  AttacherType = Attacher::AttachEngine3D
  Height = 50
  Placement = pos=(2e-14,-52,0) rot=(0,0,-1;1.5708rad)
  Radius = 1.5
FEATURE [Part::Cylinder] Cylinder1159  label="Válec1159"
  Angle = 360
  AttacherType = Attacher::AttachEngine3D
  Height = 50
  Placement = pos=(36.7696,-36.7696,0) rot=(0,0,-1;0.785398rad)
  Radius = 1.5
FEATURE [Part::Cylinder] Cylinder1160  label="Válec1160"
  Angle = 360
  AttacherType = Attacher::AttachEngine3D
  Height = 50
  Placement = pos=(52,0,0) rot=(0,0,1;0rad)
  Radius = 1.5
FEATURE [Part::Cylinder] Cylinder1161  label="Válec1161"
  Angle = 360
  AttacherType = Attacher::AttachEngine3D
  Height = 50
  Placement = pos=(36.7696,36.7696,0) rot=(0,0,1;0.785398rad)
  Radius = 1.5
FEATURE [Part::Cylinder] Cylinder1162  label="Válec1162"
  Angle = 360
  AttacherType = Attacher::AttachEngine3D
  Height = 50
  Placement = pos=(-7e-15,52,0) rot=(0,0,1;1.5708rad)
  Radius = 1.5
FEATURE [Part::Cylinder] Cylinder1163  label="Válec1163"
  Angle = 360
  AttacherType = Attacher::AttachEngine3D
  Height = 50
  Placement = pos=(-36.7696,36.7696,0) rot=(0,0,1;2.35619rad)
  Radius = 1.5
FEATURE [Part::Compound] Compound880
  Links = -> [Cylinder1152,Cylinder1153,Cylinder1154,Cylinder1155,Cylinder1156,Cylinder1157,Cylinder1158,Cylinder1159]
  Placement = pos=(0,0,-7) rot=(0,0,1;0rad)
FEATURE [Part::Cut] Cut430
  Base = -> Compound878
  Tool = -> Compound880
FEATURE [Part::Cylinder] Cylinder1164  label="Válec1164"
  Angle = 360
  AttacherType = Attacher::AttachEngine3D
  Height = 50
  Placement = pos=(-52,-2.1e-14,0) rot=(0,0,1;3.14159rad)
  Radius = 1.5
FEATURE [Part::Cylinder] Cylinder1165  label="Válec1165"
  Angle = 360
  AttacherType = Attacher::AttachEngine3D
  Height = 50
  Placement = pos=(-36.7696,-36.7696,0) rot=(0,0,1;3.92699rad)
  Radius = 1.5
FEATURE [Part::Cylinder] Cylinder1166  label="Válec1166"
  Angle = 360
  AttacherType = Attacher::AttachEngine3D
  Height = 50
  Placement = pos=(2e-14,-52,0) rot=(0,0,-1;1.5708rad)
  Radius = 1.5
FEATURE [Part::Cylinder] Cylinder1167  label="Válec1167"
  Angle = 360
  AttacherType = Attacher::AttachEngine3D
  Height = 50
  Placement = pos=(36.7696,-36.7696,0) rot=(0,0,-1;0.785398rad)
  Radius = 1.5
FEATURE [Part::Compound] Compound879
  Links = -> [Cylinder1160,Cylinder1161,Cylinder1162,Cylinder1163,Cylinder1164,Cylinder1165,Cylinder1166,Cylinder1167]
  Placement = pos=(0,0,-7) rot=(0,0,1;0rad)
FEATURE [Part::Cut] Cut431
  Base = -> Cut429
  Tool = -> Compound879
FEATURE [Part::Box] Box459  label="Krychle459"
  AttacherType = Attacher::AttachEngine3D
  Height = 2
  Length = 8
  Placement = pos=(47,-3,34) rot=(0,0,1;0rad)
  Width = 6
FEATURE [Part::Box] Box460  label="Krychle460"
  AttacherType = Attacher::AttachEngine3D
  Height = 2
  Length = 8
  Placement = pos=(35.3553,31.1127,34) rot=(0,0,1;0.785398rad)
  Width = 6
FEATURE [Part::Box] Box461  label="Krychle461"
  AttacherType = Attacher::AttachEngine3D
  Height = 2
  Length = 8
  Placement = pos=(3,47,34) rot=(0,0,1;1.5708rad)
  Width = 6
FEATURE [Part::Box] Box462  label="Krychle462"
  AttacherType = Attacher::AttachEngine3D
  Height = 2
  Length = 8
  Placement = pos=(-31.1127,35.3553,34) rot=(0,0,1;2.35619rad)
  Width = 6
FEATURE [Part::Box] Box463  label="Krychle463"
  AttacherType = Attacher::AttachEngine3D
  Height = 2
  Length = 8
  Placement = pos=(-47,3,34) rot=(0,0,1;3.14159rad)
  Width = 6
FEATURE [Part::Box] Box464  label="Krychle464"
  AttacherType = Attacher::AttachEngine3D
  Height = 2
  Length = 8
  Placement = pos=(-35.3553,-31.1127,34) rot=(0,0,1;3.92699rad)
  Width = 6
FEATURE [Part::Box] Box465  label="Krychle465"
  AttacherType = Attacher::AttachEngine3D
  Height = 2
  Length = 8
  Placement = pos=(-3,-47,34) rot=(0,0,-1;1.5708rad)
  Width = 6
FEATURE [Part::Box] Box466  label="Krychle466"
  AttacherType = Attacher::AttachEngine3D
  Height = 2
  Length = 8
  Placement = pos=(31.1127,-35.3553,34) rot=(0,0,-1;0.785398rad)
  Width = 6
FEATURE [Part::Compound] Compound881
  Links = -> [Box459,Box460,Box461,Box462,Box463,Box464,Box465,Box466]
  Placement = pos=(0,0,1) rot=(0,0,1;0rad)
FEATURE [Part::Box] Box467  label="Krychle467"
  AttacherType = Attacher::AttachEngine3D
  Height = 2
  Length = 8
  Placement = pos=(47,-3,34) rot=(0,0,1;0rad)
  Width = 6
FEATURE [Part::Box] Box468  label="Krychle468"
  AttacherType = Attacher::AttachEngine3D
  Height = 2
  Length = 8
  Placement = pos=(35.3553,31.1127,34) rot=(0,0,1;0.785398rad)
  Width = 6
FEATURE [Part::Box] Box469  label="Krychle469"
  AttacherType = Attacher::AttachEngine3D
  Height = 2
  Length = 8
  Placement = pos=(3,47,34) rot=(0,0,1;1.5708rad)
  Width = 6
FEATURE [Part::Box] Box470  label="Krychle470"
  AttacherType = Attacher::AttachEngine3D
  Height = 2
  Length = 8
  Placement = pos=(-31.1127,35.3553,34) rot=(0,0,1;2.35619rad)
  Width = 6
FEATURE [Part::Box] Box471  label="Krychle471"
  AttacherType = Attacher::AttachEngine3D
  Height = 2
  Length = 8
  Placement = pos=(-47,3,34) rot=(0,0,1;3.14159rad)
  Width = 6
FEATURE [Part::Box] Box472  label="Krychle472"
  AttacherType = Attacher::AttachEngine3D
  Height = 2
  Length = 8
  Placement = pos=(-35.3553,-31.1127,34) rot=(0,0,1;3.92699rad)
  Width = 6
FEATURE [Part::Box] Box473  label="Krychle473"
  AttacherType = Attacher::AttachEngine3D
  Height = 2
  Length = 8
  Placement = pos=(-3,-47,34) rot=(0,0,-1;1.5708rad)
  Width = 6
FEATURE [Part::Box] Box474  label="Krychle474"
  AttacherType = Attacher::AttachEngine3D
  Height = 2
  Length = 8
  Placement = pos=(31.1127,-35.3553,34) rot=(0,0,-1;0.785398rad)
  Width = 6
FEATURE [Part::Compound] Compound882
  Links = -> [Box467,Box468,Box469,Box470,Box471,Box472,Box473,Box474]
  Placement = pos=(0,0,1) rot=(0,0,1;0rad)
FEATURE [Part::Cut] Cut432
  Base = -> Cut431
  Tool = -> Compound881
FEATURE [Part::Cut] Cut433
  Base = -> Cut430
  Tool = -> Compound882
FEATURE [Part::Box] Box475  label="Krychle475"
  AttacherType = Attacher::AttachEngine3D
  Height = 6
  Length = 2
  Placement = pos=(32,48,24) rot=(0,0,1;0rad)
  Width = 6
FEATURE [Part::Box] Box476  label="Krychle476"
  AttacherType = Attacher::AttachEngine3D
  Height = 6
  Length = 2
  Placement = pos=(32,-54,24) rot=(0,0,1;0rad)
  Width = 6
FEATURE [Part::Box] Box477  label="Krychle477"
  AttacherType = Attacher::AttachEngine3D
  Height = 6
  Length = 2
  Placement = pos=(38,33,39) rot=(0,0,1;0rad)
  Width = 6
FEATURE [Part::Box] Box478  label="Krychle478"
  AttacherType = Attacher::AttachEngine3D
  Height = 6
  Length = 2
  Placement = pos=(38,-39,39) rot=(0,0,1;0rad)
  Width = 6
FEATURE [Part::Compound] Compound884
  Links = -> [Box475,Box476,Box477,Box478]
FEATURE [Part::Cylinder] Cylinder1168  label="Válec1168"
  Angle = 360
  AttacherType = Attacher::AttachEngine3D
  Height = 100
  Placement = pos=(34,-36,42) rot=(0,1,0;1.5708rad)
  Radius = 1.5
FEATURE [Part::Cylinder] Cylinder1169  label="Válec1169"
  Angle = 360
  AttacherType = Attacher::AttachEngine3D
  Height = 100
  Placement = pos=(24,51,27) rot=(0,1,0;1.5708rad)
  Radius = 1.5
FEATURE [Part::Cylinder] Cylinder1170  label="Válec1170"
  Angle = 360
  AttacherType = Attacher::AttachEngine3D
  Height = 100
  Placement = pos=(24,-51,27) rot=(0,1,0;1.5708rad)
  Radius = 1.5
FEATURE [Part::Cylinder] Cylinder1171  label="Válec1171"
  Angle = 360
  AttacherType = Attacher::AttachEngine3D
  Height = 100
  Placement = pos=(34,36,42) rot=(0,1,0;1.5708rad)
  Radius = 1.5
FEATURE [Part::Compound] Compound883
  Links = -> [Cylinder1169,Cylinder1170,Cylinder1171,Cylinder1168]
FEATURE [Part::Box] Box479  label="Krychle479"
  AttacherType = Attacher::AttachEngine3D
  Height = 25
  Length = 46
  Placement = pos=(0,-54,20) rot=(0,0,1;0rad)
  Width = 108
FEATURE [Part::Cylinder] Cylinder1172  label="Válec1172"
  Angle = 360
  AttacherType = Attacher::AttachEngine3D
  Height = 25
  Placement = pos=(0,0,20) rot=(0,0,1;0rad)
  Radius = 47
FEATURE [Part::Cut] Cut434
  Base = -> Box479
  Tool = -> Cylinder1172
FEATURE [Part::Box] Box480  label="Krychle480"
  AttacherType = Attacher::AttachEngine3D
  Height = 25
  Length = 46
  Placement = pos=(0,-54,20) rot=(0,0,1;0rad)
  Width = 108
FEATURE [Part::Cylinder] Cylinder1173  label="Válec1173"
  Angle = 360
  AttacherType = Attacher::AttachEngine3D
  Height = 25
  Placement = pos=(0,0,20) rot=(0,0,1;0rad)
  Radius = 47
FEATURE [Part::Cut] Cut435
  Base = -> Box480
  Tool = -> Cylinder1173
FEATURE [Part::FeaturePython] Tube110  label="ZKL-61816-4"  # WARN: FeaturePython — macro-defined, semantics opaque (R4)
  AttacherType = Attacher::AttachEngine3D
  Height = 10
  InnerRadius = 40
  OuterRadius = 50
  Placement = pos=(0,0,20) rot=(0,0,1;0rad)
FEATURE [Part::Cut] Cut436
  Base = -> Cut435
  Tool = -> Tube110
FEATURE [Part::Box] Box481  label="Krychle481"
  AttacherType = Attacher::AttachEngine3D
  Height = 25
  Length = 46
  Placement = pos=(0,-54,20) rot=(0,0,1;0rad)
  Width = 108
FEATURE [Part::Cylinder] Cylinder1174  label="Válec1174"
  Angle = 360
  AttacherType = Attacher::AttachEngine3D
  Height = 25
  Placement = pos=(0,0,20) rot=(0,0,1;0rad)
  Radius = 47
FEATURE [Part::Cut] Cut437
  Base = -> Box481
  Tool = -> Cylinder1174
FEATURE [Part::FeaturePython] Tube111  label="ZKL-61816-004"  # WARN: FeaturePython — macro-defined, semantics opaque (R4)
  AttacherType = Attacher::AttachEngine3D
  Height = 11
  InnerRadius = 40
  OuterRadius = 50
  Placement = pos=(0,0,20) rot=(0,0,1;0rad)
FEATURE [Part::Cut] Cut438
  Base = -> Cut437
  Tool = -> Tube111
FEATURE [Part::Cylinder] Cylinder1175  label="Válec1175"
  Angle = 360
  AttacherType = Attacher::AttachEngine3D
  Height = 50
  Placement = pos=(52,0,0) rot=(0,0,1;0rad)
  Radius = 1.5
FEATURE [Part::Cylinder] Cylinder1176  label="Válec1176"
  Angle = 360
  AttacherType = Attacher::AttachEngine3D
  Height = 50
  Placement = pos=(36.7696,36.7696,0) rot=(0,0,1;0.785398rad)
  Radius = 1.5
FEATURE [Part::Cylinder] Cylinder1177  label="Válec1177"
  Angle = 360
  AttacherType = Attacher::AttachEngine3D
  Height = 50
  Placement = pos=(-7e-15,52,0) rot=(0,0,1;1.5708rad)
  Radius = 1.5
FEATURE [Part::Cylinder] Cylinder1178  label="Válec1178"
  Angle = 360
  AttacherType = Attacher::AttachEngine3D
  Height = 50
  Placement = pos=(-36.7696,36.7696,0) rot=(0,0,1;2.35619rad)
  Radius = 1.5
FEATURE [Part::Cylinder] Cylinder1179  label="Válec1179"
  Angle = 360
  AttacherType = Attacher::AttachEngine3D
  Height = 50
  Placement = pos=(-52,-2.1e-14,0) rot=(0,0,1;3.14159rad)
  Radius = 1.5
FEATURE [Part::Cylinder] Cylinder1180  label="Válec1180"
  Angle = 360
  AttacherType = Attacher::AttachEngine3D
  Height = 50
  Placement = pos=(-36.7696,-36.7696,0) rot=(0,0,1;3.92699rad)
  Radius = 1.5
FEATURE [Part::Cylinder] Cylinder1181  label="Válec1181"
  Angle = 360
  AttacherType = Attacher::AttachEngine3D
  Height = 50
  Placement = pos=(2e-14,-52,0) rot=(0,0,-1;1.5708rad)
  Radius = 1.5
FEATURE [Part::Cylinder] Cylinder1182  label="Válec1182"
  Angle = 360
  AttacherType = Attacher::AttachEngine3D
  Height = 50
  Placement = pos=(36.7696,-36.7696,0) rot=(0,0,-1;0.785398rad)
  Radius = 1.5
FEATURE [Part::Compound] Compound885
  Links = -> [Cylinder1175,Cylinder1176,Cylinder1177,Cylinder1178,Cylinder1179,Cylinder1180,Cylinder1181,Cylinder1182]
  Placement = pos=(0,0,-7) rot=(0,0,1;0rad)
FEATURE [Part::Cut] Cut439
  Base = -> Cut438
  Tool = -> Compound885
FEATURE [Part::Box] Box482  label="Krychle482"
  AttacherType = Attacher::AttachEngine3D
  Height = 6
  Length = 2
  Placement = pos=(32,48,24) rot=(0,0,1;0rad)
  Width = 6
FEATURE [Part::Box] Box483  label="Krychle483"
  AttacherType = Attacher::AttachEngine3D
  Height = 6
  Length = 2
  Placement = pos=(32,-54,24) rot=(0,0,1;0rad)
  Width = 6
FEATURE [Part::Box] Box484  label="Krychle484"
  AttacherType = Attacher::AttachEngine3D
  Height = 6
  Length = 2
  Placement = pos=(38,33,39) rot=(0,0,1;0rad)
  Width = 6
FEATURE [Part::Box] Box485  label="Krychle485"
  AttacherType = Attacher::AttachEngine3D
  Height = 6
  Length = 2
  Placement = pos=(38,-39,39) rot=(0,0,1;0rad)
  Width = 6
FEATURE [Part::Compound] Compound886
  Links = -> [Box482,Box483,Box484,Box485]
FEATURE [Part::Cut] Cut440
  Base = -> Cut439
  Tool = -> Compound886
FEATURE [Part::Box] Box486  label="Krychle486"
  AttacherType = Attacher::AttachEngine3D
  Height = 6
  Length = 2
  Placement = pos=(32,48,24) rot=(0,0,1;0rad)
  Width = 6
FEATURE [Part::Box] Box487  label="Krychle487"
  AttacherType = Attacher::AttachEngine3D
  Height = 6
  Length = 2
  Placement = pos=(32,-54,24) rot=(0,0,1;0rad)
  Width = 6
FEATURE [Part::Box] Box488  label="Krychle488"
  AttacherType = Attacher::AttachEngine3D
  Height = 6
  Length = 2
  Placement = pos=(38,33,39) rot=(0,0,1;0rad)
  Width = 6
FEATURE [Part::Box] Box489  label="Krychle489"
  AttacherType = Attacher::AttachEngine3D
  Height = 6
  Length = 2
  Placement = pos=(38,-39,39) rot=(0,0,1;0rad)
  Width = 6
FEATURE [Part::Compound] Compound887
  Links = -> [Box486,Box487,Box488,Box489]
FEATURE [Part::Cut] Cut441
  Base = -> Cut433
  Tool = -> Compound887
FEATURE [Part::Box] Box490  label="Krychle490"
  AttacherType = Attacher::AttachEngine3D
  Height = 6
  Length = 2
  Placement = pos=(32,48,24) rot=(0,0,1;0rad)
  Width = 6
FEATURE [Part::Box] Box491  label="Krychle491"
  AttacherType = Attacher::AttachEngine3D
  Height = 6
  Length = 2
  Placement = pos=(32,-54,24) rot=(0,0,1;0rad)
  Width = 6
FEATURE [Part::Box] Box492  label="Krychle492"
  AttacherType = Attacher::AttachEngine3D
  Height = 6
  Length = 2
  Placement = pos=(38,33,39) rot=(0,0,1;0rad)
  Width = 6
FEATURE [Part::Box] Box493  label="Krychle493"
  AttacherType = Attacher::AttachEngine3D
  Height = 6
  Length = 2
  Placement = pos=(38,-39,39) rot=(0,0,1;0rad)
  Width = 6
FEATURE [Part::Compound] Compound888
  Links = -> [Box490,Box491,Box492,Box493]
FEATURE [Part::Cut] Cut442
  Base = -> Cut432
  Tool = -> Compound888
FEATURE [Part::Cylinder] Cylinder1183  label="Válec1183"
  Angle = 360
  AttacherType = Attacher::AttachEngine3D
  Height = 100
  Placement = pos=(34,-36,42) rot=(0,1,0;1.5708rad)
  Radius = 1.5
FEATURE [Part::Cylinder] Cylinder1184  label="Válec1184"
  Angle = 360
  AttacherType = Attacher::AttachEngine3D
  Height = 100
  Placement = pos=(24,51,27) rot=(0,1,0;1.5708rad)
  Radius = 1.5
FEATURE [Part::Cylinder] Cylinder1185  label="Válec1185"
  Angle = 360
  AttacherType = Attacher::AttachEngine3D
  Height = 100
  Placement = pos=(24,-51,27) rot=(0,1,0;1.5708rad)
  Radius = 1.5
FEATURE [Part::Cylinder] Cylinder1186  label="Válec1186"
  Angle = 360
  AttacherType = Attacher::AttachEngine3D
  Height = 100
  Placement = pos=(34,36,42) rot=(0,1,0;1.5708rad)
  Radius = 1.5
FEATURE [Part::Compound] Compound889
  Links = -> [Cylinder1184,Cylinder1185,Cylinder1186,Cylinder1183]
FEATURE [Part::Cylinder] Cylinder1187  label="Válec1187"
  Angle = 360
  AttacherType = Attacher::AttachEngine3D
  Height = 100
  Placement = pos=(34,-36,42) rot=(0,1,0;1.5708rad)
  Radius = 1.5
FEATURE [Part::Cylinder] Cylinder1188  label="Válec1188"
  Angle = 360
  AttacherType = Attacher::AttachEngine3D
  Height = 100
  Placement = pos=(24,51,27) rot=(0,1,0;1.5708rad)
  Radius = 1.5
FEATURE [Part::Cylinder] Cylinder1189  label="Válec1189"
  Angle = 360
  AttacherType = Attacher::AttachEngine3D
  Height = 100
  Placement = pos=(24,-51,27) rot=(0,1,0;1.5708rad)
  Radius = 1.5
FEATURE [Part::Cylinder] Cylinder1190  label="Válec1190"
  Angle = 360
  AttacherType = Attacher::AttachEngine3D
  Height = 100
  Placement = pos=(34,36,42) rot=(0,1,0;1.5708rad)
  Radius = 1.5
FEATURE [Part::Compound] Compound890
  Links = -> [Cylinder1188,Cylinder1189,Cylinder1190,Cylinder1187]
FEATURE [Part::Cut] Cut443
  Base = -> Cut440
  Tool = -> Compound889
FEATURE [Part::Cylinder] Cylinder1191  label="Válec1191"
  Angle = 360
  AttacherType = Attacher::AttachEngine3D
  Height = 100
  Placement = pos=(34,-36,42) rot=(0,1,0;1.5708rad)
  Radius = 1.5
FEATURE [Part::Cylinder] Cylinder1192  label="Válec1192"
  Angle = 360
  AttacherType = Attacher::AttachEngine3D
  Height = 100
  Placement = pos=(24,51,27) rot=(0,1,0;1.5708rad)
  Radius = 1.5
FEATURE [Part::Cylinder] Cylinder1193  label="Válec1193"
  Angle = 360
  AttacherType = Attacher::AttachEngine3D
  Height = 100
  Placement = pos=(24,-51,27) rot=(0,1,0;1.5708rad)
  Radius = 1.5
FEATURE [Part::Cylinder] Cylinder1194  label="Válec1194"
  Angle = 360
  AttacherType = Attacher::AttachEngine3D
  Height = 100
  Placement = pos=(34,36,42) rot=(0,1,0;1.5708rad)
  Radius = 1.5
FEATURE [Part::Compound] Compound891
  Links = -> [Cylinder1192,Cylinder1193,Cylinder1194,Cylinder1191]
FEATURE [Part::Cut] Cut444
  Base = -> Cut442
  Tool = -> Compound890
FEATURE [Part::Cut] Cut445
  Base = -> Cut441
  Tool = -> Compound891
FEATURE [Part::Cylinder] Cylinder1195  label="Válec1195"
  Angle = 360
  AttacherType = Attacher::AttachEngine3D
  Height = 50
  Placement = pos=(52,0,0) rot=(0,0,1;0rad)
  Radius = 1.5
FEATURE [Part::Cylinder] Cylinder1196  label="Válec1196"
  Angle = 360
  AttacherType = Attacher::AttachEngine3D
  Height = 50
  Placement = pos=(36.7696,36.7696,0) rot=(0,0,1;0.785398rad)
  Radius = 1.5
FEATURE [Part::Cylinder] Cylinder1197  label="Válec1197"
  Angle = 360
  AttacherType = Attacher::AttachEngine3D
  Height = 50
  Placement = pos=(-7e-15,52,0) rot=(0,0,1;1.5708rad)
  Radius = 1.5
FEATURE [Part::Cylinder] Cylinder1198  label="Válec1198"
  Angle = 360
  AttacherType = Attacher::AttachEngine3D
  Height = 50
  Placement = pos=(-36.7696,36.7696,0) rot=(0,0,1;2.35619rad)
  Radius = 1.5
FEATURE [Part::Cylinder] Cylinder1199  label="Válec1199"
  Angle = 360
  AttacherType = Attacher::AttachEngine3D
  Height = 50
  Placement = pos=(-52,-2.1e-14,0) rot=(0,0,1;3.14159rad)
  Radius = 1.5
FEATURE [Part::Cylinder] Cylinder1200  label="Válec1200"
  Angle = 360
  AttacherType = Attacher::AttachEngine3D
  Height = 50
  Placement = pos=(-36.7696,-36.7696,0) rot=(0,0,1;3.92699rad)
  Radius = 1.5
FEATURE [Part::Cylinder] Cylinder1201  label="Válec1201"
  Angle = 360
  AttacherType = Attacher::AttachEngine3D
  Height = 50
  Placement = pos=(2e-14,-52,0) rot=(0,0,-1;1.5708rad)
  Radius = 1.5
FEATURE [Part::Cylinder] Cylinder1202  label="Válec1202"
  Angle = 360
  AttacherType = Attacher::AttachEngine3D
  Height = 50
  Placement = pos=(36.7696,-36.7696,0) rot=(0,0,-1;0.785398rad)
  Radius = 1.5
FEATURE [Part::Compound] Compound892
  Links = -> [Cylinder1195,Cylinder1196,Cylinder1197,Cylinder1198,Cylinder1199,Cylinder1200,Cylinder1201,Cylinder1202]
  Placement = pos=(0,0,-7) rot=(0,0,1;0rad)
FEATURE [Part::Cylinder] Cylinder1203  label="Válec1203"
  Angle = 360
  AttacherType = Attacher::AttachEngine3D
  Height = 50
  Placement = pos=(52,0,0) rot=(0,0,1;0rad)
  Radius = 1.5
FEATURE [Part::Cylinder] Cylinder1204  label="Válec1204"
  Angle = 360
  AttacherType = Attacher::AttachEngine3D
  Height = 50
  Placement = pos=(36.7696,36.7696,0) rot=(0,0,1;0.785398rad)
  Radius = 1.5
FEATURE [Part::Cylinder] Cylinder1205  label="Válec1205"
  Angle = 360
  AttacherType = Attacher::AttachEngine3D
  Height = 50
  Placement = pos=(-7e-15,52,0) rot=(0,0,1;1.5708rad)
  Radius = 1.5
FEATURE [Part::Cylinder] Cylinder1206  label="Válec1206"
  Angle = 360
  AttacherType = Attacher::AttachEngine3D
  Height = 50
  Placement = pos=(-36.7696,36.7696,0) rot=(0,0,1;2.35619rad)
  Radius = 1.5
FEATURE [Part::Cylinder] Cylinder1207  label="Válec1207"
  Angle = 360
  AttacherType = Attacher::AttachEngine3D
  Height = 50
  Placement = pos=(-52,-2.1e-14,0) rot=(0,0,1;3.14159rad)
  Radius = 1.5
FEATURE [Part::Cylinder] Cylinder1208  label="Válec1208"
  Angle = 360
  AttacherType = Attacher::AttachEngine3D
  Height = 50
  Placement = pos=(-36.7696,-36.7696,0) rot=(0,0,1;3.92699rad)
  Radius = 1.5
FEATURE [Part::Cylinder] Cylinder1209  label="Válec1209"
  Angle = 360
  AttacherType = Attacher::AttachEngine3D
  Height = 50
  Placement = pos=(2e-14,-52,0) rot=(0,0,-1;1.5708rad)
  Radius = 1.5
FEATURE [Part::Cylinder] Cylinder1210  label="Válec1210"
  Angle = 360
  AttacherType = Attacher::AttachEngine3D
  Height = 50
  Placement = pos=(36.7696,-36.7696,0) rot=(0,0,-1;0.785398rad)
  Radius = 1.5
FEATURE [Part::Compound] Compound893
  Links = -> [Cylinder1203,Cylinder1204,Cylinder1205,Cylinder1206,Cylinder1207,Cylinder1208,Cylinder1209,Cylinder1210]
  Placement = pos=(0,0,-7) rot=(0,0,1;0rad)
FEATURE [Part::Box] Box494  label="Krychle494"
  AttacherType = Attacher::AttachEngine3D
  Height = 2
  Length = 8
  Placement = pos=(47,-3,34) rot=(0,0,1;0rad)
  Width = 6
FEATURE [Part::Box] Box495  label="Krychle495"
  AttacherType = Attacher::AttachEngine3D
  Height = 2
  Length = 8
  Placement = pos=(35.3553,31.1127,34) rot=(0,0,1;0.785398rad)
  Width = 6
FEATURE [Part::Box] Box496  label="Krychle496"
  AttacherType = Attacher::AttachEngine3D
  Height = 2
  Length = 8
  Placement = pos=(3,47,34) rot=(0,0,1;1.5708rad)
  Width = 6
FEATURE [Part::Box] Box497  label="Krychle497"
  AttacherType = Attacher::AttachEngine3D
  Height = 2
  Length = 8
  Placement = pos=(-31.1127,35.3553,34) rot=(0,0,1;2.35619rad)
  Width = 6
FEATURE [Part::Box] Box498  label="Krychle498"
  AttacherType = Attacher::AttachEngine3D
  Height = 2
  Length = 8
  Placement = pos=(-47,3,34) rot=(0,0,1;3.14159rad)
  Width = 6
FEATURE [Part::Box] Box499  label="Krychle499"
  AttacherType = Attacher::AttachEngine3D
  Height = 2
  Length = 8
  Placement = pos=(-35.3553,-31.1127,34) rot=(0,0,1;3.92699rad)
  Width = 6
FEATURE [Part::Box] Box500  label="Krychle500"
  AttacherType = Attacher::AttachEngine3D
  Height = 2
  Length = 8
  Placement = pos=(-3,-47,34) rot=(0,0,-1;1.5708rad)
  Width = 6
FEATURE [Part::Box] Box501  label="Krychle501"
  AttacherType = Attacher::AttachEngine3D
  Height = 2
  Length = 8
  Placement = pos=(31.1127,-35.3553,34) rot=(0,0,-1;0.785398rad)
  Width = 6
FEATURE [Part::Compound] Compound894
  Links = -> [Box494,Box495,Box496,Box497,Box498,Box499,Box500,Box501]
FEATURE [Part::Box] Box502  label="Krychle502"
  AttacherType = Attacher::AttachEngine3D
  Height = 2
  Length = 8
  Placement = pos=(47,-3,34) rot=(0,0,1;0rad)
  Width = 6
FEATURE [Part::Box] Box503  label="Krychle503"
  AttacherType = Attacher::AttachEngine3D
  Height = 2
  Length = 8
  Placement = pos=(35.3553,31.1127,34) rot=(0,0,1;0.785398rad)
  Width = 6
FEATURE [Part::Box] Box504  label="Krychle504"
  AttacherType = Attacher::AttachEngine3D
  Height = 2
  Length = 8
  Placement = pos=(3,47,34) rot=(0,0,1;1.5708rad)
  Width = 6
FEATURE [Part::Box] Box505  label="Krychle505"
  AttacherType = Attacher::AttachEngine3D
  Height = 2
  Length = 8
  Placement = pos=(-31.1127,35.3553,34) rot=(0,0,1;2.35619rad)
  Width = 6
FEATURE [Part::Box] Box506  label="Krychle506"
  AttacherType = Attacher::AttachEngine3D
  Height = 2
  Length = 8
  Placement = pos=(-47,3,34) rot=(0,0,1;3.14159rad)
  Width = 6
FEATURE [Part::Box] Box507  label="Krychle507"
  AttacherType = Attacher::AttachEngine3D
  Height = 2
  Length = 8
  Placement = pos=(-35.3553,-31.1127,34) rot=(0,0,1;3.92699rad)
  Width = 6
FEATURE [Part::Box] Box508  label="Krychle508"
  AttacherType = Attacher::AttachEngine3D
  Height = 2
  Length = 8
  Placement = pos=(-3,-47,34) rot=(0,0,-1;1.5708rad)
  Width = 6
FEATURE [Part::Box] Box509  label="Krychle509"
  AttacherType = Attacher::AttachEngine3D
  Height = 2
  Length = 8
  Placement = pos=(31.1127,-35.3553,34) rot=(0,0,-1;0.785398rad)
  Width = 6
FEATURE [Part::Compound] Compound895
  Links = -> [Box502,Box503,Box504,Box505,Box506,Box507,Box508,Box509]
  Placement = pos=(0,0,1) rot=(0,0,1;0rad)
FEATURE [Part::Cut] Cut446
  Base = -> Cut443
  Tool = -> Compound895
FEATURE [Part::Compound] Compound896  label="J-midi_deep-thin-ring"
  Links = -> [Cut444,Cut446,Cut445]
FEATURE [Part::Cylinder] Cylinder714  label="Válec714"
  Angle = 360
  AttacherType = Attacher::AttachEngine3D
  Height = 60
  Placement = pos=(41,0,-54) rot=(0,0,1;0rad)
  Radius = 1.5
FEATURE [Part::Cylinder] Cylinder715  label="Válec715"
  Angle = 360
  AttacherType = Attacher::AttachEngine3D
  Height = 40
  Placement = pos=(202,50,-28) rot=(0,0,1;0rad)
  Radius = 12
FEATURE [Part::Box] Box334  label="Krychle334"
  AttacherType = Attacher::AttachEngine3D
  Height = 2
  Length = 8
  Placement = pos=(37,-3,-4) rot=(0,0,1;0rad)
  Width = 6
FEATURE [Part::Cylinder] Cylinder717  label="Válec717"
  Angle = 360
  AttacherType = Attacher::AttachEngine3D
  Height = 12
  Radius = 46
FEATURE [Part::Cylinder] Cylinder721  label="Válec721"
  Angle = 360
  AttacherType = Attacher::AttachEngine3D
  Height = 40
  Placement = pos=(214,56,-30) rot=(0,0,1;0rad)
  Radius = 12
FEATURE [Part::Box] Box335  label="Krychle335"
  AttacherType = Attacher::AttachEngine3D
  Height = 28
  Length = 6
  Placement = pos=(26,28,-8) rot=(0,0,1;0rad)
  Width = 10
FEATURE [Part::Cylinder] Cylinder718  label="Válec718"
  Angle = 360
  AttacherType = Attacher::AttachEngine3D
  Height = 40
  Placement = pos=(256,0,-30) rot=(0,0,1;0rad)
  Radius = 10
FEATURE [Part::Cylinder] Cylinder720  label="Válec720"
  Angle = 360
  AttacherType = Attacher::AttachEngine3D
  Height = 40
  Placement = pos=(202,50,-28) rot=(0,0,1;0rad)
  Radius = 12
FEATURE [Part::Box] Box339  label="Krychle339"
  AttacherType = Attacher::AttachEngine3D
  Height = 2
  Length = 8
  Placement = pos=(28.2843,24.0416,-4) rot=(0,0,1;0.785398rad)
  Width = 6
FEATURE [Part::Box] Box341  label="Krychle341"
  AttacherType = Attacher::AttachEngine3D
  Height = 28
  Length = 6
  Placement = pos=(26,28,-8) rot=(0,0,1;0rad)
  Width = 10
FEATURE [Part::Box] Box336  label="Krychle336"
  AttacherType = Attacher::AttachEngine3D
  Height = 32
  Length = 8
  Placement = pos=(238,0,-8) rot=(0,0,1;0rad)
  Width = 38
FEATURE [Part::Box] Box338  label="Krychle338"
  AttacherType = Attacher::AttachEngine3D
  Height = 32
  Length = 8
  Placement = pos=(238,0,-8) rot=(0,0,1;0rad)
  Width = 38
FEATURE [Part::Box] Box342  label="Krychle342"
  AttacherType = Attacher::AttachEngine3D
  Height = 32
  Length = 46
  Placement = pos=(200,38,-8) rot=(0,0,1;0rad)
  Width = 16
FEATURE [Part::Compound] Compound709
  Links = -> [Box336,Box342]
FEATURE [Part::Box] Box340  label="Krychle340"
  AttacherType = Attacher::AttachEngine3D
  Height = 2
  Length = 8
  Placement = pos=(-28.2843,-24.0416,-4) rot=(0,0,1;3.92699rad)
  Width = 6
FEATURE [Part::Box] Box343  label="Krychle343"
  AttacherType = Attacher::AttachEngine3D
  Height = 28
  Length = 6
  Placement = pos=(32,24,-8) rot=(0,0,1;0rad)
  Width = 14
FEATURE [Part::Compound] Compound712
  Links = -> [Box335,Box343]
FEATURE [Part::Cylinder] Cylinder716  label="Válec716"
  Angle = 360
  AttacherType = Attacher::AttachEngine3D
  Height = 40
  Placement = pos=(214,56,-30) rot=(0,0,1;0rad)
  Radius = 12
FEATURE [Part::Compound] Compound713
  Links = -> [Cylinder718,Cylinder716]
  Placement = pos=(0,0,2) rot=(0,0,1;0rad)
FEATURE [Part::Cut] Cut340
  Base = -> Compound709
  Tool = -> Compound713
FEATURE [Part::Cut] Cut331
  Base = -> Cut340
  Placement = pos=(-200,0,0) rot=(0,0,1;0rad)
  Tool = -> Cylinder720
FEATURE [Part::Box] Box337  label="Krychle337"
  AttacherType = Attacher::AttachEngine3D
  Height = 28
  Length = 6
  Placement = pos=(32,24,-8) rot=(0,0,1;0rad)
  Width = 14
FEATURE [Part::Compound] Compound705
  Links = -> [Box341,Box337]
FEATURE [Part::Compound] Compound708
  Links = -> [Cut331,Compound705]
FEATURE [Part::Cylinder] Cylinder719  label="Válec719"
  Angle = 360
  AttacherType = Attacher::AttachEngine3D
  Height = 12
  Radius = 54
FEATURE [Part::Cylinder] Cylinder725  label="Válec725"
  Angle = 360
  AttacherType = Attacher::AttachEngine3D
  Height = 60
  Placement = pos=(-41,-1.1e-14,-54) rot=(0,0,1;3.14159rad)
  Radius = 1.5
FEATURE [Part::Cylinder] Cylinder727  label="Válec727"
  Angle = 360
  AttacherType = Attacher::AttachEngine3D
  Height = 60
  Placement = pos=(-28.9914,-28.9914,-54) rot=(0,0,1;3.92699rad)
  Radius = 1.5
FEATURE [Part::Box] Box344  label="Krychle344"
  AttacherType = Attacher::AttachEngine3D
  Height = 2
  Length = 8
  Placement = pos=(3,37,-4) rot=(0,0,1;1.5708rad)
  Width = 6
FEATURE [Part::Box] Box348  label="Krychle348"
  AttacherType = Attacher::AttachEngine3D
  Height = 2
  Length = 8
  Placement = pos=(37,-3,-4) rot=(0,0,1;0rad)
  Width = 6
FEATURE [Part::Box] Box349  label="Krychle349"
  AttacherType = Attacher::AttachEngine3D
  Height = 2
  Length = 8
  Placement = pos=(-37,3,-4) rot=(0,0,1;3.14159rad)
  Width = 6
FEATURE [Part::Cylinder] Cylinder728  label="Válec728"
  Angle = 360
  AttacherType = Attacher::AttachEngine3D
  Height = 60
  Placement = pos=(28.9914,-28.9914,-54) rot=(0,0,-1;0.785398rad)
  Radius = 1.5
FEATURE [Part::Cylinder] Cylinder729  label="Válec729"
  Angle = 360
  AttacherType = Attacher::AttachEngine3D
  Height = 60
  Placement = pos=(41,0,-54) rot=(0,0,1;0rad)
  Radius = 1.5
FEATURE [Part::Cylinder] Cylinder723  label="Válec723"
  Angle = 360
  AttacherType = Attacher::AttachEngine3D
  Height = 60
  Placement = pos=(28.9914,28.9914,-54) rot=(0,0,1;0.785398rad)
  Radius = 1.5
FEATURE [Part::Cylinder] Cylinder730  label="Válec730"
  Angle = 360
  AttacherType = Attacher::AttachEngine3D
  Height = 60
  Placement = pos=(1.2e-14,-41,-54) rot=(0,0,-1;1.5708rad)
  Radius = 1.5
FEATURE [Part::Box] Box345  label="Krychle345"
  AttacherType = Attacher::AttachEngine3D
  Height = 32
  Length = 46
  Placement = pos=(200,38,-8) rot=(0,0,1;0rad)
  Width = 16
FEATURE [Part::Compound] Compound706
  Links = -> [Box338,Box345]
FEATURE [Part::Box] Box347  label="Krychle347"
  AttacherType = Attacher::AttachEngine3D
  Height = 2
  Length = 8
  Placement = pos=(-3,-37,-4) rot=(0,0,-1;1.5708rad)
  Width = 6
FEATURE [Part::Box] Box350  label="Krychle350"
  AttacherType = Attacher::AttachEngine3D
  Height = 2
  Length = 8
  Placement = pos=(28.2843,24.0416,-4) rot=(0,0,1;0.785398rad)
  Width = 6
FEATURE [Part::Cylinder] Cylinder722  label="Válec722"
  Angle = 360
  AttacherType = Attacher::AttachEngine3D
  Height = 40
  Placement = pos=(256,0,-30) rot=(0,0,1;0rad)
  Radius = 10
FEATURE [Part::Compound] Compound711
  Links = -> [Cylinder722,Cylinder721]
  Placement = pos=(0,0,2) rot=(0,0,1;0rad)
FEATURE [Part::Cut] Cut337
  Base = -> Compound706
  Tool = -> Compound711
FEATURE [Part::Cut] Cut345
  Base = -> Cut337
  Placement = pos=(-200,0,0) rot=(0,0,1;0rad)
  Tool = -> Cylinder715
FEATURE [Part::Compound] Compound714
  Links = -> [Cut345,Compound712]
FEATURE [Part::Mirroring] mirror012  label="Compound196 (mirrored)001"
  Base = (0,0,0)
  Normal = (1e-16,-1,0)
  Source = -> Compound714
FEATURE [Part::Box] Box346  label="Krychle346"
  AttacherType = Attacher::AttachEngine3D
  Height = 2
  Length = 8
  Placement = pos=(24.0416,-28.2843,-4) rot=(0,0,-1;0.785398rad)
  Width = 6
FEATURE [Part::Cylinder] Cylinder726  label="Válec726"
  Angle = 360
  AttacherType = Attacher::AttachEngine3D
  Height = 60
  Placement = pos=(1.2e-14,-41,-54) rot=(0,0,-1;1.5708rad)
  Radius = 1.5
FEATURE [Part::Cylinder] Cylinder724  label="Válec724"
  Angle = 360
  AttacherType = Attacher::AttachEngine3D
  Height = 60
  Placement = pos=(28.9914,-28.9914,-54) rot=(0,0,-1;0.785398rad)
  Radius = 1.5
FEATURE [Part::Box] Box354  label="Krychle354"
  AttacherType = Attacher::AttachEngine3D
  Height = 2
  Length = 8
  Placement = pos=(-24.0416,28.2843,-4) rot=(0,0,1;2.35619rad)
  Width = 6
FEATURE [Part::Box] Box355  label="Krychle355"
  AttacherType = Attacher::AttachEngine3D
  Height = 2
  Length = 8
  Placement = pos=(24.0416,-28.2843,-4) rot=(0,0,-1;0.785398rad)
  Width = 6
FEATURE [Part::Box] Box352  label="Krychle352"
  AttacherType = Attacher::AttachEngine3D
  Height = 2
  Length = 8
  Placement = pos=(-3,-37,-4) rot=(0,0,-1;1.5708rad)
  Width = 6
FEATURE [Part::Box] Box353  label="Krychle353"
  AttacherType = Attacher::AttachEngine3D
  Height = 2
  Length = 8
  Placement = pos=(-24.0416,28.2843,-4) rot=(0,0,1;2.35619rad)
  Width = 6
FEATURE [Part::Cylinder] Cylinder736  label="Válec736"
  Angle = 360
  AttacherType = Attacher::AttachEngine3D
  Height = 60
  Placement = pos=(-28.9914,28.9914,-54) rot=(0,0,1;2.35619rad)
  Radius = 1.5
FEATURE [Part::Cylinder] Cylinder731  label="Válec731"
  Angle = 360
  AttacherType = Attacher::AttachEngine3D
  Height = 60
  Placement = pos=(-4e-15,41,-54) rot=(0,0,1;1.5708rad)
  Radius = 1.5
FEATURE [Part::Box] Box356  label="Krychle356"
  AttacherType = Attacher::AttachEngine3D
  Height = 2
  Length = 8
  Placement = pos=(3,37,-4) rot=(0,0,1;1.5708rad)
  Width = 6
FEATURE [Part::Cylinder] Cylinder734  label="Válec734"
  Angle = 360
  AttacherType = Attacher::AttachEngine3D
  Height = 60
  Placement = pos=(-41,-1.1e-14,-54) rot=(0,0,1;3.14159rad)
  Radius = 1.5
FEATURE [Part::Cylinder] Cylinder738  label="Válec738"
  Angle = 360
  AttacherType = Attacher::AttachEngine3D
  Height = 60
  Placement = pos=(-28.9914,-28.9914,-54) rot=(0,0,1;3.92699rad)
  Radius = 1.5
FEATURE [Part::Cylinder] Cylinder735  label="Válec735"
  Angle = 360
  AttacherType = Attacher::AttachEngine3D
  Height = 60
  Placement = pos=(28.9914,28.9914,-54) rot=(0,0,1;0.785398rad)
  Radius = 1.5
FEATURE [Part::Cylinder] Cylinder732  label="Válec732"
  Angle = 360
  AttacherType = Attacher::AttachEngine3D
  Height = 60
  Placement = pos=(-28.9914,28.9914,-54) rot=(0,0,1;2.35619rad)
  Radius = 1.5
FEATURE [Part::Cylinder] Cylinder737  label="Válec737"
  Angle = 360
  AttacherType = Attacher::AttachEngine3D
  Height = 60
  Placement = pos=(-4e-15,41,-54) rot=(0,0,1;1.5708rad)
  Radius = 1.5
FEATURE [Part::Cylinder] Cylinder739  label="Válec739"
  Angle = 360
  AttacherType = Attacher::AttachEngine3D
  Height = 60
  Placement = pos=(28,-51,7) rot=(0,1,0;1.5708rad)
  Radius = 1.5
FEATURE [Part::Cylinder] Cylinder740  label="Válec740"
  Angle = 360
  AttacherType = Attacher::AttachEngine3D
  Height = 60
  Placement = pos=(-4e-15,41,-54) rot=(0,0,1;1.5708rad)
  Radius = 1.5
FEATURE [Part::Box] Box351  label="Krychle351"
  AttacherType = Attacher::AttachEngine3D
  Height = 2
  Length = 8
  Placement = pos=(-28.2843,-24.0416,-4) rot=(0,0,1;3.92699rad)
  Width = 6
FEATURE [Part::Cylinder] Cylinder733  label="Válec733"
  Angle = 360
  AttacherType = Attacher::AttachEngine3D
  Height = 60
  Placement = pos=(28.9914,-28.9914,-54) rot=(0,0,-1;0.785398rad)
  Radius = 1.5
FEATURE [Part::Box] Box362  label="Krychle362"
  AttacherType = Attacher::AttachEngine3D
  Height = 6
  Length = 2
  Placement = pos=(36,-24,-8) rot=(0,0,1;0rad)
  Width = 6
FEATURE [Part::Cylinder] Cylinder747  label="Válec747"
  Angle = 360
  AttacherType = Attacher::AttachEngine3D
  Height = 60
  Placement = pos=(32,-21,-5) rot=(0,1,0;1.5708rad)
  Radius = 1.5
FEATURE [Part::Cylinder] Cylinder744  label="Válec744"
  Angle = 360
  AttacherType = Attacher::AttachEngine3D
  Height = 60
  Placement = pos=(-28.9914,-28.9914,-54) rot=(0,0,1;3.92699rad)
  Radius = 1.5
FEATURE [Part::Cylinder] Cylinder742  label="Válec742"
  Angle = 360
  AttacherType = Attacher::AttachEngine3D
  Height = 60
  Placement = pos=(28,51,7) rot=(0,1,0;1.5708rad)
  Radius = 1.5
FEATURE [Part::Cylinder] Cylinder748  label="Válec748"
  Angle = 360
  AttacherType = Attacher::AttachEngine3D
  Height = 60
  Placement = pos=(1.2e-14,-41,-54) rot=(0,0,-1;1.5708rad)
  Radius = 1.5
FEATURE [Part::Box] Box357  label="Krychle357"
  AttacherType = Attacher::AttachEngine3D
  Height = 2
  Length = 8
  Placement = pos=(-37,3,-4) rot=(0,0,1;3.14159rad)
  Width = 6
FEATURE [Part::Box] Box363  label="Krychle363"
  AttacherType = Attacher::AttachEngine3D
  Height = 6
  Length = 2
  Placement = pos=(32,48,4) rot=(0,0,1;0rad)
  Width = 6
FEATURE [Part::Cylinder] Cylinder749  label="Válec749"
  Angle = 360
  AttacherType = Attacher::AttachEngine3D
  Height = 60
  Placement = pos=(28.9914,28.9914,-54) rot=(0,0,1;0.785398rad)
  Radius = 1.5
FEATURE [Part::Box] Box358  label="Krychle358"
  AttacherType = Attacher::AttachEngine3D
  Height = 6
  Length = 2
  Placement = pos=(36,18,-8) rot=(0,0,1;0rad)
  Width = 6
FEATURE [Part::Box] Box359  label="Krychle359"
  AttacherType = Attacher::AttachEngine3D
  Height = 6
  Length = 2
  Placement = pos=(32,-54,4) rot=(0,0,1;0rad)
  Width = 6
FEATURE [Part::Compound] Compound703
  Links = -> [Box358,Box362,Box363,Box359]
FEATURE [Part::Cylinder] Cylinder741  label="Válec741"
  Angle = 360
  AttacherType = Attacher::AttachEngine3D
  Height = 50
  Placement = pos=(-50,-2.3e-14,-15) rot=(0,0,1;3.14159rad)
  Radius = 1.5
FEATURE [Part::Box] Box360  label="Krychle360"
  AttacherType = Attacher::AttachEngine3D
  Height = 6
  Length = 2
  Placement = pos=(36,20,-8) rot=(0,0,1;0rad)
  Width = 6
FEATURE [Part::Cylinder] Cylinder746  label="Válec746"
  Angle = 360
  AttacherType = Attacher::AttachEngine3D
  Height = 60
  Placement = pos=(-28.9914,28.9914,-54) rot=(0,0,1;2.35619rad)
  Radius = 1.5
FEATURE [Part::Cylinder] Cylinder745  label="Válec745"
  Angle = 360
  AttacherType = Attacher::AttachEngine3D
  Height = 60
  Placement = pos=(28,-51,7) rot=(0,1,0;1.5708rad)
  Radius = 1.5
FEATURE [Part::Cylinder] Cylinder743  label="Válec743"
  Angle = 360
  AttacherType = Attacher::AttachEngine3D
  Height = 60
  Placement = pos=(41,0,-54) rot=(0,0,1;0rad)
  Radius = 1.5
FEATURE [Part::Box] Box361  label="Krychle361"
  AttacherType = Attacher::AttachEngine3D
  Height = 6
  Length = 2
  Placement = pos=(32,-54,4) rot=(0,0,1;0rad)
  Width = 6
FEATURE [Part::Box] Box365  label="Krychle365"
  AttacherType = Attacher::AttachEngine3D
  Height = 6
  Length = 2
  Placement = pos=(36,-26,-8) rot=(0,0,1;0rad)
  Width = 6
FEATURE [Part::Cylinder] Cylinder760  label="Válec760"
  Angle = 360
  AttacherType = Attacher::AttachEngine3D
  Height = 60
  Placement = pos=(32,-23,-5) rot=(0,1,0;1.5708rad)
  Radius = 1.5
FEATURE [Part::Cylinder] Cylinder750  label="Válec750"
  Angle = 360
  AttacherType = Attacher::AttachEngine3D
  Height = 60
  Placement = pos=(32,21,-5) rot=(0,1,0;1.5708rad)
  Radius = 1.5
FEATURE [Part::Compound] Compound710
  Links = -> [Cylinder750,Cylinder747,Cylinder742,Cylinder739]
FEATURE [Part::Cylinder] Cylinder751  label="Válec751"
  Angle = 360
  AttacherType = Attacher::AttachEngine3D
  Height = 60
  Placement = pos=(-41,-1.1e-14,-54) rot=(0,0,1;3.14159rad)
  Radius = 1.5
FEATURE [Part::Box] Box364  label="Krychle364"
  AttacherType = Attacher::AttachEngine3D
  Height = 6
  Length = 2
  Placement = pos=(32,48,4) rot=(0,0,1;0rad)
  Width = 6
FEATURE [Part::Cylinder] Cylinder753  label="Válec753"
  Angle = 360
  AttacherType = Attacher::AttachEngine3D
  Height = 60
  Placement = pos=(32,23,-5) rot=(0,1,0;1.5708rad)
  Radius = 1.5
FEATURE [Part::Cylinder] Cylinder756  label="Válec756"
  Angle = 360
  AttacherType = Attacher::AttachEngine3D
  Height = 50
  Placement = pos=(35.3553,-35.3553,-15) rot=(0,0,-1;0.785398rad)
  Radius = 1.5
FEATURE [Part::Cylinder] Cylinder754  label="Válec754"
  Angle = 360
  AttacherType = Attacher::AttachEngine3D
  Height = 50
  Placement = pos=(2.5e-14,-50,-15) rot=(0,0,-1;1.5708rad)
  Radius = 1.5
FEATURE [Part::Box] Box366  label="Krychle366"
  AttacherType = Attacher::AttachEngine3D
  Height = 6
  Length = 2
  Placement = pos=(36,20,-8) rot=(0,0,1;0rad)
  Width = 6
FEATURE [Part::Cylinder] Cylinder752  label="Válec752"
  Angle = 360
  AttacherType = Attacher::AttachEngine3D
  Height = 50
  Placement = pos=(50,0,-15) rot=(0,0,1;0rad)
  Radius = 1.5
FEATURE [Part::Cylinder] Cylinder755  label="Válec755"
  Angle = 360
  AttacherType = Attacher::AttachEngine3D
  Height = 50
  Placement = pos=(-35.3553,-35.3553,-15) rot=(0,0,1;3.92699rad)
  Radius = 1.5
FEATURE [Part::Cylinder] Cylinder757  label="Válec757"
  Angle = 360
  AttacherType = Attacher::AttachEngine3D
  Height = 60
  Placement = pos=(28,51,7) rot=(0,1,0;1.5708rad)
  Radius = 1.5
FEATURE [Part::Cylinder] Cylinder759  label="Válec759"
  Angle = 360
  AttacherType = Attacher::AttachEngine3D
  Height = 50
  Placement = pos=(35.3553,35.3553,-15) rot=(0,0,1;0.785398rad)
  Radius = 1.5
FEATURE [Part::Box] Box369  label="Krychle369"
  AttacherType = Attacher::AttachEngine3D
  Height = 6
  Length = 2
  Placement = pos=(36,-54,4) rot=(0,0,1;0rad)
  Width = 6
FEATURE [Part::Box] Box367  label="Krychle367"
  AttacherType = Attacher::AttachEngine3D
  Height = 6
  Length = 2
  Placement = pos=(36,-26,-8) rot=(0,0,1;0rad)
  Width = 6
FEATURE [Part::Cylinder] Cylinder773  label="Válec773"
  Angle = 360
  AttacherType = Attacher::AttachEngine3D
  Height = 50
  Placement = pos=(35.36,35.36,-40) rot=(0,0,1;0.785398rad)
  Radius = 4
FEATURE [Part::Cylinder] Cylinder766  label="Válec766"
  Angle = 360
  AttacherType = Attacher::AttachEngine3D
  Height = 50
  Placement = pos=(-35.3553,35.3553,-15) rot=(0,0,1;2.35619rad)
  Radius = 1.5
FEATURE [Part::Cylinder] Cylinder767  label="Válec767"
  Angle = 360
  AttacherType = Attacher::AttachEngine3D
  Height = 50
  Placement = pos=(-7e-15,50,-15) rot=(0,0,1;1.5708rad)
  Radius = 1.5
FEATURE [Part::Cylinder] Cylinder774  label="Válec774"
  Angle = 360
  AttacherType = Attacher::AttachEngine3D
  Height = 60
  Placement = pos=(32,23,-5) rot=(0,1,0;1.5708rad)
  Radius = 1.5
FEATURE [Part::Cylinder] Cylinder769  label="Válec769"
  Angle = 360
  AttacherType = Attacher::AttachEngine3D
  Height = 60
  Placement = pos=(28,51,7) rot=(0,1,0;1.5708rad)
  Radius = 1.5
FEATURE [Part::Compound] Compound704
  Links = -> [Cylinder753,Cylinder760,Cylinder769,Cylinder745]
FEATURE [Part::Box] Box368  label="Krychle368"
  AttacherType = Attacher::AttachEngine3D
  Height = 6
  Length = 2
  Placement = pos=(36,48,4) rot=(0,0,1;0rad)
  Width = 6
FEATURE [Part::Cylinder] Cylinder770  label="Válec770"
  Angle = 360
  AttacherType = Attacher::AttachEngine3D
  Height = 60
  Placement = pos=(32,-23,-5) rot=(0,1,0;1.5708rad)
  Radius = 1.5
FEATURE [Part::Cylinder] Cylinder772  label="Válec772"
  Angle = 360
  AttacherType = Attacher::AttachEngine3D
  Height = 60
  Placement = pos=(28,-51,7) rot=(0,1,0;1.5708rad)
  Radius = 1.5
FEATURE [Part::Compound] Compound715
  Links = -> [Cylinder774,Cylinder770,Cylinder757,Cylinder772]
FEATURE [Part::Cylinder] Cylinder775  label="Válec775"
  Angle = 360
  AttacherType = Attacher::AttachEngine3D
  Height = 50
  Placement = pos=(35.36,-35.36,-40) rot=(0,0,1;0.785398rad)
  Radius = 4
FEATURE [Part::FeaturePython] wormgear041  # WARN: FeaturePython — macro-defined, semantics opaque (R4)
  AttacherType = Attacher::AttachEngine3D
  beta = 39.4866
  clearance = 0.25
  diameter = 71
  head = 0
  height = 20
  module = 1.5
  pressure_angle = 20
  reverse_pitch = false
  teeth = 39
  version = 0.0.3
FEATURE [Part::Cut] Cut338
  Base = -> Cylinder717
  Tool = -> wormgear041
FEATURE [Part::FeaturePython] wormgear040  # WARN: FeaturePython — macro-defined, semantics opaque (R4)
  AttacherType = Attacher::AttachEngine3D
  Placement = pos=(0,0,0) rot=(0,0,-1;0.107861rad)
  beta = 39.4866
  clearance = 0.25
  diameter = 71
  head = 0
  height = 20
  module = 1.5
  pressure_angle = 20
  reverse_pitch = true
  teeth = 39
  version = 0.0.3
FEATURE [Part::Cut] Cut339
  Base = -> Cylinder719
  Placement = pos=(0,0,12) rot=(0,0,1;0.034907rad)
  Tool = -> wormgear040
FEATURE [Part::Compound] Compound707
  Links = -> [Cut339,Cut338]
FEATURE [Part::FeaturePython] Tube077  # WARN: FeaturePython — macro-defined, semantics opaque (R4)
  AttacherType = Attacher::AttachEngine3D
  Height = 8
  InnerRadius = 38
  OuterRadius = 46
  Placement = pos=(0,0,-8) rot=(0,0,1;0rad)
FEATURE [Part::Compound] Compound717
  Links = -> [Cylinder749,Cylinder740,Cylinder746,Cylinder751,Cylinder744,Cylinder748,Cylinder733,Cylinder743]
  Placement = pos=(0,0,0) rot=(0,0,1;0.392699rad)
FEATURE [Part::Cut] Cut335
  Base = -> Compound707
  Tool = -> Compound717
FEATURE [Part::Cut] Cut333
  Base = -> Cut335
  Tool = -> Compound710
FEATURE [Part::Cut] Cut344
  Base = -> Cut333
  Tool = -> Compound703
FEATURE [Part::Compound] Compound719
  Links = -> [Box339,Box344,Box353,Box349,Box340,Box347,Box346,Box334]
  Placement = pos=(0,0,0) rot=(0,0,1;0.392699rad)
FEATURE [Part::Compound] Compound723
  Links = -> [Cylinder752,Cylinder759,Cylinder767,Cylinder766,Cylinder741,Cylinder755,Cylinder754,Cylinder756]
FEATURE [Part::Cut] Cut332
  Base = -> Cut344
  Tool = -> Compound723
FEATURE [Part::Compound] Compound721
  Links = -> [Cylinder773,Cylinder775]
  Placement = pos=(0,0,2) rot=(0,0,1;0rad)
FEATURE [Part::Compound] Compound724
  Links = -> [Box366,Box367,Box368,Box369]
FEATURE [Part::Compound] Compound727
  Links = -> [Cylinder723,Cylinder731,Cylinder736,Cylinder725,Cylinder727,Cylinder726,Cylinder728,Cylinder714]
  Placement = pos=(0,0,0) rot=(0,0,1;0.392699rad)
FEATURE [Part::Cut] Cut341
  Base = -> Tube077
  Tool = -> Compound727
FEATURE [Part::Compound] Compound720
  Links = -> [mirror012,Compound708]
FEATURE [Part::Compound] Compound726
  Links = -> [Cylinder735,Cylinder737,Cylinder732,Cylinder734,Cylinder738,Cylinder730,Cylinder724,Cylinder729]
  Placement = pos=(0,0,0) rot=(0,0,1;0.392699rad)
FEATURE [Part::Compound] Compound716
  Links = -> [Box350,Box356,Box354,Box357,Box351,Box352,Box355,Box348]
  Placement = pos=(0,0,0) rot=(0,0,1;0.392699rad)
FEATURE [Part::Cut] Cut342
  Base = -> Compound720
  Tool = -> Compound716
FEATURE [Part::Cut] Cut336
  Base = -> Cut342
  Tool = -> Compound726
FEATURE [Part::Compound] Compound725
  Links = -> [Box360,Box365,Box364,Box361]
FEATURE [Part::Cut] Cut350
  Base = -> Cut341
  Tool = -> Compound719
FEATURE [Part::Cut] Cut349
  Base = -> Cut350
  Tool = -> Compound725
FEATURE [Part::Cut] Cut348
  Base = -> Cut349
  Tool = -> Compound704
FEATURE [Part::Compound] Compound897  label="J-midi-deep_monoblok"
  Links = -> [Cut332,Cut348]
FEATURE [Part::Cylinder] Cylinder1211  label="Válec1211"
  Angle = 360
  AttacherType = Attacher::AttachEngine3D
  Height = 12
  Radius = 46
FEATURE [Part::Cylinder] Cylinder1212  label="Válec1212"
  Angle = 360
  AttacherType = Attacher::AttachEngine3D
  Height = 12
  Radius = 54
FEATURE [Part::FeaturePython] wormgear067  # WARN: FeaturePython — macro-defined, semantics opaque (R4)
  AttacherType = Attacher::AttachEngine3D
  beta = 39.4866
  clearance = 0.25
  diameter = 71
  head = 0
  height = 20
  module = 1.5
  pressure_angle = 20
  reverse_pitch = false
  teeth = 39
  version = 0.0.3
FEATURE [Part::Cut] Cut447
  Base = -> Cylinder1211
  Tool = -> wormgear067
FEATURE [Part::FeaturePython] wormgear068  # WARN: FeaturePython — macro-defined, semantics opaque (R4)
  AttacherType = Attacher::AttachEngine3D
  Placement = pos=(0,0,0) rot=(0,0,-1;0.107861rad)
  beta = 39.4866
  clearance = 0.25
  diameter = 71
  head = 0
  height = 20
  module = 1.5
  pressure_angle = 20
  reverse_pitch = true
  teeth = 39
  version = 0.0.3
FEATURE [Part::Cut] Cut448
  Base = -> Cylinder1212
  Placement = pos=(0,0,12) rot=(0,0,1;0.034907rad)
  Tool = -> wormgear068
FEATURE [Part::Compound] Compound898
  Links = -> [Cut448,Cut447]
FEATURE [Part::Cylinder] Cylinder1213  label="Válec1213"
  Angle = 360
  AttacherType = Attacher::AttachEngine3D
  Height = 50
  Placement = pos=(-7e-15,52,0) rot=(0,0,1;1.5708rad)
  Radius = 1.5
FEATURE [Part::Cylinder] Cylinder1214  label="Válec1214"
  Angle = 360
  AttacherType = Attacher::AttachEngine3D
  Height = 50
  Placement = pos=(52,0,0) rot=(0,0,1;0rad)
  Radius = 1.5
FEATURE [Part::Cylinder] Cylinder1215  label="Válec1215"
  Angle = 360
  AttacherType = Attacher::AttachEngine3D
  Height = 50
  Placement = pos=(36.7696,36.7696,0) rot=(0,0,1;0.785398rad)
  Radius = 1.5
FEATURE [Part::Cylinder] Cylinder1216  label="Válec1216"
  Angle = 360
  AttacherType = Attacher::AttachEngine3D
  Height = 50
  Placement = pos=(-52,-2.1e-14,0) rot=(0,0,1;3.14159rad)
  Radius = 1.5
FEATURE [Part::Cylinder] Cylinder1217  label="Válec1217"
  Angle = 360
  AttacherType = Attacher::AttachEngine3D
  Height = 50
  Placement = pos=(-36.7696,-36.7696,0) rot=(0,0,1;3.92699rad)
  Radius = 1.5
FEATURE [Part::Cylinder] Cylinder1218  label="Válec1218"
  Angle = 360
  AttacherType = Attacher::AttachEngine3D
  Height = 50
  Placement = pos=(2e-14,-52,0) rot=(0,0,-1;1.5708rad)
  Radius = 1.5
FEATURE [Part::Cylinder] Cylinder1219  label="Válec1219"
  Angle = 360
  AttacherType = Attacher::AttachEngine3D
  Height = 50
  Placement = pos=(36.7696,-36.7696,0) rot=(0,0,-1;0.785398rad)
  Radius = 1.5
FEATURE [Part::Cylinder] Cylinder1220  label="Válec1220"
  Angle = 360
  AttacherType = Attacher::AttachEngine3D
  Height = 50
  Placement = pos=(-36.7696,36.7696,0) rot=(0,0,1;2.35619rad)
  Radius = 1.5
FEATURE [Part::Compound] Compound899
  Links = -> [Cylinder1214,Cylinder1215,Cylinder1213,Cylinder1220,Cylinder1216,Cylinder1217,Cylinder1218,Cylinder1219]
  Placement = pos=(0,0,-7) rot=(0,0,1;0rad)
FEATURE [Part::Box] Box510  label="Krychle510"
  AttacherType = Attacher::AttachEngine3D
  Height = 25
  Length = 4
  Placement = pos=(51,-6,20) rot=(0,0,1;0rad)
  Width = 12
FEATURE [Part::Chamfer] Chamfer009
  Base = -> Box510
  Edges = 2 edges r=2: [Edge5,Edge7]
FEATURE [Part::Chamfer] Chamfer010
  Base = -> Box510
  Edges = 2 edges r=2: [Edge5,Edge7]
  Placement = pos=(0,0,0) rot=(0,0,1;0.785398rad)
FEATURE [Part::Chamfer] Chamfer011
  Base = -> Box510
  Edges = 2 edges r=2: [Edge5,Edge7]
  Placement = pos=(0,0,0) rot=(0,0,1;2.35619rad)
FEATURE [Part::Chamfer] Chamfer012
  Base = -> Box510
  Edges = 2 edges r=2: [Edge5,Edge7]
  Placement = pos=(0,0,0) rot=(0,0,1;1.5708rad)
FEATURE [Part::Chamfer] Chamfer013
  Base = -> Box510
  Edges = 2 edges r=2: [Edge5,Edge7]
  Placement = pos=(0,0,0) rot=(0,0,-1;0.785398rad)
FEATURE [Part::Chamfer] Chamfer014
  Base = -> Box510
  Edges = 2 edges r=2: [Edge5,Edge7]
  Placement = pos=(0,0,0) rot=(0,0,1;3.92699rad)
FEATURE [Part::Chamfer] Chamfer015
  Base = -> Box510
  Edges = 2 edges r=2: [Edge5,Edge7]
  Placement = pos=(0,0,0) rot=(0,0,-1;1.5708rad)
FEATURE [Part::Chamfer] Chamfer016
  Base = -> Box510
  Edges = 2 edges r=2: [Edge5,Edge7]
  Placement = pos=(0,0,0) rot=(0,0,1;3.14159rad)
FEATURE [Part::Compound] Compound900
  Links = -> [Chamfer009,Chamfer010,Chamfer012,Chamfer011,Chamfer016,Chamfer014,Chamfer015,Chamfer013]
FEATURE [Part::Box] Box511  label="Krychle511"
  AttacherType = Attacher::AttachEngine3D
  Height = 12
  Length = 4
  Placement = pos=(51,-6,12) rot=(0,0,1;0rad)
  Width = 12
FEATURE [Part::Chamfer] Chamfer017
  Base = -> Box511
  Edges = 2 edges r=2: [Edge5,Edge7]
FEATURE [Part::Chamfer] Chamfer018
  Base = -> Box511
  Edges = 2 edges r=2: [Edge5,Edge7]
  Placement = pos=(0,0,0) rot=(0,0,1;0.785398rad)
FEATURE [Part::Chamfer] Chamfer019
  Base = -> Box511
  Edges = 2 edges r=2: [Edge5,Edge7]
  Placement = pos=(0,0,0) rot=(0,0,1;1.5708rad)
FEATURE [Part::Chamfer] Chamfer020
  Base = -> Box511
  Edges = 2 edges r=2: [Edge5,Edge7]
  Placement = pos=(0,0,0) rot=(0,0,1;2.35619rad)
FEATURE [Part::Chamfer] Chamfer021
  Base = -> Box511
  Edges = 2 edges r=2: [Edge5,Edge7]
  Placement = pos=(0,0,0) rot=(0,0,1;3.14159rad)
FEATURE [Part::Chamfer] Chamfer022
  Base = -> Box511
  Edges = 2 edges r=2: [Edge5,Edge7]
  Placement = pos=(0,0,0) rot=(0,0,1;3.92699rad)
FEATURE [Part::Chamfer] Chamfer023
  Base = -> Box511
  Edges = 2 edges r=2: [Edge5,Edge7]
  Placement = pos=(0,0,0) rot=(0,0,-1;1.5708rad)
FEATURE [Part::Chamfer] Chamfer024
  Base = -> Box511
  Edges = 2 edges r=2: [Edge5,Edge7]
  Placement = pos=(0,0,0) rot=(0,0,-1;0.785398rad)
FEATURE [Part::Compound] Compound901
  Links = -> [Chamfer017,Chamfer018,Chamfer019,Chamfer020,Chamfer021,Chamfer022,Chamfer023,Chamfer024]
FEATURE [Part::Cut] Cut449
  Base = -> Compound901
  Tool = -> Compound899
FEATURE [Part::Cylinder] Cylinder1221  label="Válec1221"
  Angle = 360
  AttacherType = Attacher::AttachEngine3D
  Height = 50
  Placement = pos=(36.7696,36.7696,0) rot=(0,0,1;0.785398rad)
  Radius = 1.5
FEATURE [Part::Cylinder] Cylinder1222  label="Válec1222"
  Angle = 360
  AttacherType = Attacher::AttachEngine3D
  Height = 50
  Placement = pos=(36.7696,-36.7696,0) rot=(0,0,-1;0.785398rad)
  Radius = 1.5
FEATURE [Part::Cylinder] Cylinder1223  label="Válec1223"
  Angle = 360
  AttacherType = Attacher::AttachEngine3D
  Height = 50
  Placement = pos=(52,0,0) rot=(0,0,1;0rad)
  Radius = 1.5
FEATURE [Part::Cylinder] Cylinder1224  label="Válec1224"
  Angle = 360
  AttacherType = Attacher::AttachEngine3D
  Height = 50
  Placement = pos=(-52,-2.1e-14,0) rot=(0,0,1;3.14159rad)
  Radius = 1.5
FEATURE [Part::Cylinder] Cylinder1225  label="Válec1225"
  Angle = 360
  AttacherType = Attacher::AttachEngine3D
  Height = 50
  Placement = pos=(-36.7696,-36.7696,0) rot=(0,0,1;3.92699rad)
  Radius = 1.5
FEATURE [Part::Cylinder] Cylinder1226  label="Válec1226"
  Angle = 360
  AttacherType = Attacher::AttachEngine3D
  Height = 50
  Placement = pos=(-7e-15,52,0) rot=(0,0,1;1.5708rad)
  Radius = 1.5
FEATURE [Part::Cylinder] Cylinder1227  label="Válec1227"
  Angle = 360
  AttacherType = Attacher::AttachEngine3D
  Height = 50
  Placement = pos=(2e-14,-52,0) rot=(0,0,-1;1.5708rad)
  Radius = 1.5
FEATURE [Part::Cylinder] Cylinder1228  label="Válec1228"
  Angle = 360
  AttacherType = Attacher::AttachEngine3D
  Height = 50
  Placement = pos=(-36.7696,36.7696,0) rot=(0,0,1;2.35619rad)
  Radius = 1.5
FEATURE [Part::Compound] Compound902
  Links = -> [Cylinder1223,Cylinder1221,Cylinder1226,Cylinder1228,Cylinder1224,Cylinder1225,Cylinder1227,Cylinder1222]
  Placement = pos=(0,0,-7) rot=(0,0,1;0rad)
FEATURE [Part::Cut] Cut450
  Base = -> Compound898
  Tool = -> Compound902
FEATURE [Part::Cylinder] Cylinder1229  label="Válec1229"
  Angle = 360
  AttacherType = Attacher::AttachEngine3D
  Height = 50
  Placement = pos=(36.7696,36.7696,0) rot=(0,0,1;0.785398rad)
  Radius = 1.5
FEATURE [Part::Cylinder] Cylinder1230  label="Válec1230"
  Angle = 360
  AttacherType = Attacher::AttachEngine3D
  Height = 50
  Placement = pos=(36.7696,-36.7696,0) rot=(0,0,-1;0.785398rad)
  Radius = 1.5
FEATURE [Part::Cylinder] Cylinder1231  label="Válec1231"
  Angle = 360
  AttacherType = Attacher::AttachEngine3D
  Height = 50
  Placement = pos=(52,0,0) rot=(0,0,1;0rad)
  Radius = 1.5
FEATURE [Part::Cylinder] Cylinder1232  label="Válec1232"
  Angle = 360
  AttacherType = Attacher::AttachEngine3D
  Height = 50
  Placement = pos=(-52,-2.1e-14,0) rot=(0,0,1;3.14159rad)
  Radius = 1.5
FEATURE [Part::Cylinder] Cylinder1233  label="Válec1233"
  Angle = 360
  AttacherType = Attacher::AttachEngine3D
  Height = 50
  Placement = pos=(-36.7696,-36.7696,0) rot=(0,0,1;3.92699rad)
  Radius = 1.5
FEATURE [Part::Cylinder] Cylinder1234  label="Válec1234"
  Angle = 360
  AttacherType = Attacher::AttachEngine3D
  Height = 50
  Placement = pos=(-7e-15,52,0) rot=(0,0,1;1.5708rad)
  Radius = 1.5
FEATURE [Part::Cylinder] Cylinder1235  label="Válec1235"
  Angle = 360
  AttacherType = Attacher::AttachEngine3D
  Height = 50
  Placement = pos=(2e-14,-52,0) rot=(0,0,-1;1.5708rad)
  Radius = 1.5
FEATURE [Part::Cylinder] Cylinder1236  label="Válec1236"
  Angle = 360
  AttacherType = Attacher::AttachEngine3D
  Height = 50
  Placement = pos=(-36.7696,36.7696,0) rot=(0,0,1;2.35619rad)
  Radius = 1.5
FEATURE [Part::Compound] Compound722
  Links = -> [Cylinder1231,Cylinder1229,Cylinder1234,Cylinder1236,Cylinder1232,Cylinder1233,Cylinder1235,Cylinder1230]
FEATURE [Part::Cut] Cut346
  Base = -> Cut336
  Tool = -> Compound722
FEATURE [Part::Cut] Cut334
  Base = -> Cut346
  Tool = -> Compound724
FEATURE [Part::Cut] Cut343
  Base = -> Cut334
  Tool = -> Compound715
FEATURE [Part::Cut] Cut347
  Base = -> Cut343
  Tool = -> Compound721
FEATURE [Part::Compound] Compound903
  Placement = pos=(0,0,-7) rot=(0,0,1;0rad)
FEATURE [Part::Cylinder] Cylinder1237  label="Válec1237"
  Angle = 360
  AttacherType = Attacher::AttachEngine3D
  Height = 40
  Placement = pos=(214,56,-30) rot=(0,0,1;0rad)
  Radius = 12
FEATURE [Part::Cylinder] Cylinder1238  label="Válec1238"
  Angle = 360
  AttacherType = Attacher::AttachEngine3D
  Height = 40
  Placement = pos=(202,50,-28) rot=(0,0,1;0rad)
  Radius = 12
FEATURE [Part::Cylinder] Cylinder1239  label="Válec1239"
  Angle = 360
  AttacherType = Attacher::AttachEngine3D
  Height = 40
  Placement = pos=(202,50,-28) rot=(0,0,1;0rad)
  Radius = 12
FEATURE [Part::Box] Box512  label="Krychle512"
  AttacherType = Attacher::AttachEngine3D
  Height = 28
  Length = 6
  Placement = pos=(26,28,-8) rot=(0,0,1;0rad)
  Width = 10
FEATURE [Part::Cylinder] Cylinder1240  label="Válec1240"
  Angle = 360
  AttacherType = Attacher::AttachEngine3D
  Height = 40
  Placement = pos=(256,0,-30) rot=(0,0,1;0rad)
  Radius = 10
FEATURE [Part::Box] Box513  label="Krychle513"
  AttacherType = Attacher::AttachEngine3D
  Height = 32
  Length = 8
  Placement = pos=(238,0,-8) rot=(0,0,1;0rad)
  Width = 38
FEATURE [Part::Box] Box514  label="Krychle514"
  AttacherType = Attacher::AttachEngine3D
  Height = 2
  Length = 8
  Placement = pos=(37,-3,-4) rot=(0,0,1;0rad)
  Width = 6
FEATURE [Part::Box] Box515  label="Krychle515"
  AttacherType = Attacher::AttachEngine3D
  Height = 28
  Length = 6
  Placement = pos=(32,24,-8) rot=(0,0,1;0rad)
  Width = 14
FEATURE [Part::Cylinder] Cylinder1241  label="Válec1241"
  Angle = 360
  AttacherType = Attacher::AttachEngine3D
  Height = 40
  Placement = pos=(214,56,-30) rot=(0,0,1;0rad)
  Radius = 12
FEATURE [Part::Box] Box516  label="Krychle516"
  AttacherType = Attacher::AttachEngine3D
  Height = 32
  Length = 46
  Placement = pos=(200,38,-8) rot=(0,0,1;0rad)
  Width = 16
FEATURE [Part::Box] Box517  label="Krychle517"
  AttacherType = Attacher::AttachEngine3D
  Height = 32
  Length = 8
  Placement = pos=(238,0,-8) rot=(0,0,1;0rad)
  Width = 38
FEATURE [Part::Box] Box518  label="Krychle518"
  AttacherType = Attacher::AttachEngine3D
  Height = 28
  Length = 6
  Placement = pos=(26,28,-8) rot=(0,0,1;0rad)
  Width = 10
FEATURE [Part::Box] Box519  label="Krychle519"
  AttacherType = Attacher::AttachEngine3D
  Height = 28
  Length = 6
  Placement = pos=(32,24,-8) rot=(0,0,1;0rad)
  Width = 14
FEATURE [Part::Compound] Compound908
  Links = -> [Box512,Box515]
FEATURE [Part::Compound] Compound909
  Links = -> [Cylinder1240,Cylinder1241]
  Placement = pos=(0,0,2) rot=(0,0,1;0rad)
FEATURE [Part::Compound] Compound911
  Links = -> [Box517,Box516]
FEATURE [Part::Compound] Compound914
  Links = -> [Box518,Box519]
FEATURE [Part::Cut] Cut452
  Base = -> Compound911
  Tool = -> Compound909
FEATURE [Part::Cut] Cut457
  Base = -> Cut452
  Placement = pos=(-200,0,0) rot=(0,0,1;0rad)
  Tool = -> Cylinder1238
FEATURE [Part::Compound] Compound912
  Links = -> [Cut457,Compound914]
FEATURE [Part::Cylinder] Cylinder1242  label="Válec1242"
  Angle = 360
  AttacherType = Attacher::AttachEngine3D
  Height = 60
  Placement = pos=(1.2e-14,-41,-54) rot=(0,0,-1;1.5708rad)
  Radius = 1.5
FEATURE [Part::Box] Box520  label="Krychle520"
  AttacherType = Attacher::AttachEngine3D
  Height = 2
  Length = 8
  Placement = pos=(3,37,-4) rot=(0,0,1;1.5708rad)
  Width = 6
FEATURE [Part::Box] Box521  label="Krychle521"
  AttacherType = Attacher::AttachEngine3D
  Height = 2
  Length = 8
  Placement = pos=(28.2843,24.0416,-4) rot=(0,0,1;0.785398rad)
  Width = 6
FEATURE [Part::Box] Box522  label="Krychle522"
  AttacherType = Attacher::AttachEngine3D
  Height = 2
  Length = 8
  Placement = pos=(-24.0416,28.2843,-4) rot=(0,0,1;2.35619rad)
  Width = 6
FEATURE [Part::Box] Box523  label="Krychle523"
  AttacherType = Attacher::AttachEngine3D
  Height = 2
  Length = 8
  Placement = pos=(-3,-37,-4) rot=(0,0,-1;1.5708rad)
  Width = 6
FEATURE [Part::Cylinder] Cylinder1243  label="Válec1243"
  Angle = 360
  AttacherType = Attacher::AttachEngine3D
  Height = 40
  Placement = pos=(256,0,-30) rot=(0,0,1;0rad)
  Radius = 10
FEATURE [Part::Compound] Compound913
  Links = -> [Cylinder1243,Cylinder1237]
  Placement = pos=(0,0,2) rot=(0,0,1;0rad)
FEATURE [Part::Box] Box524  label="Krychle524"
  AttacherType = Attacher::AttachEngine3D
  Height = 32
  Length = 46
  Placement = pos=(200,38,-8) rot=(0,0,1;0rad)
  Width = 16
FEATURE [Part::Compound] Compound910
  Links = -> [Box513,Box524]
FEATURE [Part::Cut] Cut453
  Base = -> Compound910
  Tool = -> Compound913
FEATURE [Part::Cut] Cut455
  Base = -> Cut453
  Placement = pos=(-200,0,0) rot=(0,0,1;0rad)
  Tool = -> Cylinder1239
FEATURE [Part::Compound] Compound907
  Links = -> [Cut455,Compound908]
FEATURE [Part::Mirroring] mirror013  label="Compound196 (mirrored)002"
  Base = (0,0,0)
  Normal = (1e-16,-1,0)
  Source = -> Compound907
FEATURE [Part::Compound] Compound917
  Links = -> [mirror013,Compound912]
FEATURE [Part::Cylinder] Cylinder1244  label="Válec1244"
  Angle = 360
  AttacherType = Attacher::AttachEngine3D
  Height = 60
  Placement = pos=(28.9914,-28.9914,-54) rot=(0,0,-1;0.785398rad)
  Radius = 1.5
FEATURE [Part::Cylinder] Cylinder1245  label="Válec1245"
  Angle = 360
  AttacherType = Attacher::AttachEngine3D
  Height = 60
  Placement = pos=(41,0,-54) rot=(0,0,1;0rad)
  Radius = 1.5
FEATURE [Part::Box] Box525  label="Krychle525"
  AttacherType = Attacher::AttachEngine3D
  Height = 2
  Length = 8
  Placement = pos=(24.0416,-28.2843,-4) rot=(0,0,-1;0.785398rad)
  Width = 6
FEATURE [Part::Cylinder] Cylinder1246  label="Válec1246"
  Angle = 360
  AttacherType = Attacher::AttachEngine3D
  Height = 60
  Placement = pos=(28.9914,28.9914,-54) rot=(0,0,1;0.785398rad)
  Radius = 1.5
FEATURE [Part::Box] Box526  label="Krychle526"
  AttacherType = Attacher::AttachEngine3D
  Height = 2
  Length = 8
  Placement = pos=(-37,3,-4) rot=(0,0,1;3.14159rad)
  Width = 6
FEATURE [Part::Cylinder] Cylinder1247  label="Válec1247"
  Angle = 360
  AttacherType = Attacher::AttachEngine3D
  Height = 60
  Placement = pos=(-28.9914,28.9914,-54) rot=(0,0,1;2.35619rad)
  Radius = 1.5
FEATURE [Part::Box] Box527  label="Krychle527"
  AttacherType = Attacher::AttachEngine3D
  Height = 2
  Length = 8
  Placement = pos=(-28.2843,-24.0416,-4) rot=(0,0,1;3.92699rad)
  Width = 6
FEATURE [Part::Compound] Compound918
  Links = -> [Box521,Box520,Box522,Box526,Box527,Box523,Box525,Box514]
  Placement = pos=(0,0,0) rot=(0,0,1;0.392699rad)
FEATURE [Part::Cut] Cut454
  Base = -> Compound917
  Tool = -> Compound918
FEATURE [Part::Cylinder] Cylinder1248  label="Válec1248"
  Angle = 360
  AttacherType = Attacher::AttachEngine3D
  Height = 60
  Placement = pos=(-4e-15,41,-54) rot=(0,0,1;1.5708rad)
  Radius = 1.5
FEATURE [Part::Cylinder] Cylinder1249  label="Válec1249"
  Angle = 360
  AttacherType = Attacher::AttachEngine3D
  Height = 60
  Placement = pos=(-28.9914,-28.9914,-54) rot=(0,0,1;3.92699rad)
  Radius = 1.5
FEATURE [Part::Cylinder] Cylinder1250  label="Válec1250"
  Angle = 360
  AttacherType = Attacher::AttachEngine3D
  Height = 60
  Placement = pos=(-41,-1.1e-14,-54) rot=(0,0,1;3.14159rad)
  Radius = 1.5
FEATURE [Part::Compound] Compound906
  Links = -> [Cylinder1246,Cylinder1248,Cylinder1247,Cylinder1250,Cylinder1249,Cylinder1242,Cylinder1244,Cylinder1245]
  Placement = pos=(0,0,0) rot=(0,0,1;0.392699rad)
FEATURE [Part::Cut] Cut458
  Base = -> Cut454
  Tool = -> Compound906
FEATURE [Part::Cylinder] Cylinder1251  label="Válec1251"
  Angle = 360
  AttacherType = Attacher::AttachEngine3D
  Height = 60
  Placement = pos=(30,51,7) rot=(0,1,0;1.5708rad)
  Radius = 1.5
FEATURE [Part::Box] Box528  label="Krychle528"
  AttacherType = Attacher::AttachEngine3D
  Height = 6
  Length = 2
  Placement = pos=(36,-54,4) rot=(0,0,1;0rad)
  Width = 6
FEATURE [Part::Box] Box529  label="Krychle529"
  AttacherType = Attacher::AttachEngine3D
  Height = 6
  Length = 2
  Placement = pos=(36,-26,-8) rot=(0,0,1;0rad)
  Width = 6
FEATURE [Part::Box] Box530  label="Krychle530"
  AttacherType = Attacher::AttachEngine3D
  Height = 6
  Length = 2
  Placement = pos=(36,20,-8) rot=(0,0,1;0rad)
  Width = 6
FEATURE [Part::Cylinder] Cylinder1252  label="Válec1252"
  Angle = 360
  AttacherType = Attacher::AttachEngine3D
  Height = 50
  Placement = pos=(36.77,36.77,-40) rot=(0,0,1;0.785398rad)
  Radius = 4
FEATURE [Part::Cylinder] Cylinder1253  label="Válec1253"
  Angle = 360
  AttacherType = Attacher::AttachEngine3D
  Height = 60
  Placement = pos=(32,23,-5) rot=(0,1,0;1.5708rad)
  Radius = 1.5
FEATURE [Part::Cylinder] Cylinder1254  label="Válec1254"
  Angle = 360
  AttacherType = Attacher::AttachEngine3D
  Height = 60
  Placement = pos=(32,-23,-5) rot=(0,1,0;1.5708rad)
  Radius = 1.5
FEATURE [Part::Cylinder] Cylinder1255  label="Válec1255"
  Angle = 360
  AttacherType = Attacher::AttachEngine3D
  Height = 60
  Placement = pos=(30,-51,7) rot=(0,1,0;1.5708rad)
  Radius = 1.5
FEATURE [Part::Compound] Compound904
  Links = -> [Cylinder1253,Cylinder1254,Cylinder1251,Cylinder1255]
FEATURE [Part::Cylinder] Cylinder1256  label="Válec1256"
  Angle = 360
  AttacherType = Attacher::AttachEngine3D
  Height = 50
  Placement = pos=(36.77,-36.77,-40) rot=(0,0,1;0.785398rad)
  Radius = 4
FEATURE [Part::Compound] Compound905
  Links = -> [Cylinder1252,Cylinder1256]
  Placement = pos=(0,0,2) rot=(0,0,1;0rad)
FEATURE [Part::Box] Box531  label="Krychle531"
  AttacherType = Attacher::AttachEngine3D
  Height = 6
  Length = 2
  Placement = pos=(36,48,4) rot=(0,0,1;0rad)
  Width = 6
FEATURE [Part::Compound] Compound916
  Links = -> [Box530,Box529,Box531,Box528]
FEATURE [Part::Cylinder] Cylinder1257  label="Válec1257"
  Angle = 360
  AttacherType = Attacher::AttachEngine3D
  Height = 50
  Placement = pos=(-36.7696,36.7696,0) rot=(0,0,1;2.35619rad)
  Radius = 1.5
FEATURE [Part::Cylinder] Cylinder1258  label="Válec1258"
  Angle = 360
  AttacherType = Attacher::AttachEngine3D
  Height = 50
  Placement = pos=(36.7696,36.7696,0) rot=(0,0,1;0.785398rad)
  Radius = 1.5
FEATURE [Part::Cylinder] Cylinder1259  label="Válec1259"
  Angle = 360
  AttacherType = Attacher::AttachEngine3D
  Height = 50
  Placement = pos=(36.7696,-36.7696,0) rot=(0,0,-1;0.785398rad)
  Radius = 1.5
FEATURE [Part::Cylinder] Cylinder1260  label="Válec1260"
  Angle = 360
  AttacherType = Attacher::AttachEngine3D
  Height = 50
  Placement = pos=(-52,-2.1e-14,0) rot=(0,0,1;3.14159rad)
  Radius = 1.5
FEATURE [Part::Cylinder] Cylinder1261  label="Válec1261"
  Angle = 360
  AttacherType = Attacher::AttachEngine3D
  Height = 50
  Placement = pos=(-36.7696,-36.7696,0) rot=(0,0,1;3.92699rad)
  Radius = 1.5
FEATURE [Part::Cylinder] Cylinder1262  label="Válec1262"
  Angle = 360
  AttacherType = Attacher::AttachEngine3D
  Height = 50
  Placement = pos=(52,0,0) rot=(0,0,1;0rad)
  Radius = 1.5
FEATURE [Part::Cylinder] Cylinder1263  label="Válec1263"
  Angle = 360
  AttacherType = Attacher::AttachEngine3D
  Height = 50
  Placement = pos=(-7e-15,52,0) rot=(0,0,1;1.5708rad)
  Radius = 1.5
FEATURE [Part::Cylinder] Cylinder1264  label="Válec1264"
  Angle = 360
  AttacherType = Attacher::AttachEngine3D
  Height = 50
  Placement = pos=(2e-14,-52,0) rot=(0,0,-1;1.5708rad)
  Radius = 1.5
FEATURE [Part::Compound] Compound915
  Links = -> [Cylinder1262,Cylinder1258,Cylinder1263,Cylinder1257,Cylinder1260,Cylinder1261,Cylinder1264,Cylinder1259]
FEATURE [Part::Cut] Cut459
  Base = -> Cut458
  Tool = -> Compound915
FEATURE [Part::Cut] Cut456
  Base = -> Cut459
  Tool = -> Compound916
FEATURE [Part::Cut] Cut451
  Base = -> Cut456
  Tool = -> Compound904
FEATURE [Part::Cut] Cut460
  Base = -> Cut451
  Tool = -> Compound905
FEATURE [Part::Fillet] Fillet
  Base = -> Cut460
  Edges = 2 edges r=12: [Edge85,Edge296]
FEATURE [Part::Cylinder] Cylinder1265  label="Válec1265"
  Angle = 360
  AttacherType = Attacher::AttachEngine3D
  Height = 60
  Placement = pos=(41,0,-54) rot=(0,0,1;0rad)
  Radius = 1.5
FEATURE [Part::Box] Box532  label="Krychle532"
  AttacherType = Attacher::AttachEngine3D
  Height = 2
  Length = 8
  Placement = pos=(37,-3,-4) rot=(0,0,1;0rad)
  Width = 6
FEATURE [Part::Cylinder] Cylinder1266  label="Válec1266"
  Angle = 360
  AttacherType = Attacher::AttachEngine3D
  Height = 60
  Placement = pos=(-41,-1.1e-14,-54) rot=(0,0,1;3.14159rad)
  Radius = 1.5
FEATURE [Part::Cylinder] Cylinder1267  label="Válec1267"
  Angle = 360
  AttacherType = Attacher::AttachEngine3D
  Height = 60
  Placement = pos=(-28.9914,-28.9914,-54) rot=(0,0,1;3.92699rad)
  Radius = 1.5
FEATURE [Part::Box] Box533  label="Krychle533"
  AttacherType = Attacher::AttachEngine3D
  Height = 2
  Length = 8
  Placement = pos=(3,37,-4) rot=(0,0,1;1.5708rad)
  Width = 6
FEATURE [Part::Box] Box534  label="Krychle534"
  AttacherType = Attacher::AttachEngine3D
  Height = 2
  Length = 8
  Placement = pos=(-37,3,-4) rot=(0,0,1;3.14159rad)
  Width = 6
FEATURE [Part::Cylinder] Cylinder1268  label="Válec1268"
  Angle = 360
  AttacherType = Attacher::AttachEngine3D
  Height = 60
  Placement = pos=(28.9914,-28.9914,-54) rot=(0,0,-1;0.785398rad)
  Radius = 1.5
FEATURE [Part::Box] Box535  label="Krychle535"
  AttacherType = Attacher::AttachEngine3D
  Height = 2
  Length = 8
  Placement = pos=(28.2843,24.0416,-4) rot=(0,0,1;0.785398rad)
  Width = 6
FEATURE [Part::Box] Box536  label="Krychle536"
  AttacherType = Attacher::AttachEngine3D
  Height = 2
  Length = 8
  Placement = pos=(-28.2843,-24.0416,-4) rot=(0,0,1;3.92699rad)
  Width = 6
FEATURE [Part::Cylinder] Cylinder1269  label="Válec1269"
  Angle = 360
  AttacherType = Attacher::AttachEngine3D
  Height = 60
  Placement = pos=(28.9914,28.9914,-54) rot=(0,0,1;0.785398rad)
  Radius = 1.5
FEATURE [Part::Box] Box537  label="Krychle537"
  AttacherType = Attacher::AttachEngine3D
  Height = 2
  Length = 8
  Placement = pos=(-3,-37,-4) rot=(0,0,-1;1.5708rad)
  Width = 6
FEATURE [Part::Box] Box538  label="Krychle538"
  AttacherType = Attacher::AttachEngine3D
  Height = 2
  Length = 8
  Placement = pos=(24.0416,-28.2843,-4) rot=(0,0,-1;0.785398rad)
  Width = 6
FEATURE [Part::Cylinder] Cylinder1270  label="Válec1270"
  Angle = 360
  AttacherType = Attacher::AttachEngine3D
  Height = 60
  Placement = pos=(1.2e-14,-41,-54) rot=(0,0,-1;1.5708rad)
  Radius = 1.5
FEATURE [Part::Box] Box539  label="Krychle539"
  AttacherType = Attacher::AttachEngine3D
  Height = 2
  Length = 8
  Placement = pos=(-24.0416,28.2843,-4) rot=(0,0,1;2.35619rad)
  Width = 6
FEATURE [Part::Compound] Compound921
  Links = -> [Box535,Box533,Box539,Box534,Box536,Box537,Box538,Box532]
  Placement = pos=(0,0,0) rot=(0,0,1;0.392699rad)
FEATURE [Part::Cylinder] Cylinder1271  label="Válec1271"
  Angle = 360
  AttacherType = Attacher::AttachEngine3D
  Height = 60
  Placement = pos=(-28.9914,28.9914,-54) rot=(0,0,1;2.35619rad)
  Radius = 1.5
FEATURE [Part::Cylinder] Cylinder1272  label="Válec1272"
  Angle = 360
  AttacherType = Attacher::AttachEngine3D
  Height = 60
  Placement = pos=(-4e-15,41,-54) rot=(0,0,1;1.5708rad)
  Radius = 1.5
FEATURE [Part::Compound] Compound919
  Links = -> [Cylinder1269,Cylinder1272,Cylinder1271,Cylinder1266,Cylinder1267,Cylinder1270,Cylinder1268,Cylinder1265]
  Placement = pos=(0,0,0) rot=(0,0,1;0.392699rad)
FEATURE [Part::Box] Box540  label="Krychle540"
  AttacherType = Attacher::AttachEngine3D
  Height = 6
  Length = 2
  Placement = pos=(36,20,-8) rot=(0,0,1;0rad)
  Width = 6
FEATURE [Part::Cylinder] Cylinder1273  label="Válec1273"
  Angle = 360
  AttacherType = Attacher::AttachEngine3D
  Height = 60
  Placement = pos=(28,-51,7) rot=(0,1,0;1.5708rad)
  Radius = 1.5
FEATURE [Part::Cylinder] Cylinder1274  label="Válec1274"
  Angle = 360
  AttacherType = Attacher::AttachEngine3D
  Height = 60
  Placement = pos=(32,-23,-5) rot=(0,1,0;1.5708rad)
  Radius = 1.5
FEATURE [Part::Cylinder] Cylinder1275  label="Válec1275"
  Angle = 360
  AttacherType = Attacher::AttachEngine3D
  Height = 60
  Placement = pos=(32,23,-5) rot=(0,1,0;1.5708rad)
  Radius = 1.5
FEATURE [Part::Box] Box541  label="Krychle541"
  AttacherType = Attacher::AttachEngine3D
  Height = 6
  Length = 2
  Placement = pos=(32,-54,4) rot=(0,0,1;0rad)
  Width = 6
FEATURE [Part::Box] Box542  label="Krychle542"
  AttacherType = Attacher::AttachEngine3D
  Height = 6
  Length = 2
  Placement = pos=(32,48,4) rot=(0,0,1;0rad)
  Width = 6
FEATURE [Part::Box] Box543  label="Krychle543"
  AttacherType = Attacher::AttachEngine3D
  Height = 6
  Length = 2
  Placement = pos=(36,-26,-8) rot=(0,0,1;0rad)
  Width = 6
FEATURE [Part::Compound] Compound922
  Links = -> [Box540,Box543,Box542,Box541]
FEATURE [Part::FeaturePython] Tube112  # WARN: FeaturePython — macro-defined, semantics opaque (R4)
  AttacherType = Attacher::AttachEngine3D
  Height = 8
  InnerRadius = 38
  OuterRadius = 46
  Placement = pos=(0,0,-8) rot=(0,0,1;0rad)
FEATURE [Part::Cut] Cut461
  Base = -> Tube112
  Tool = -> Compound919
FEATURE [Part::Cylinder] Cylinder1276  label="Válec1276"
  Angle = 360
  AttacherType = Attacher::AttachEngine3D
  Height = 60
  Placement = pos=(28,51,7) rot=(0,1,0;1.5708rad)
  Radius = 1.5
FEATURE [Part::Compound] Compound920
  Links = -> [Cylinder1275,Cylinder1274,Cylinder1276,Cylinder1273]
FEATURE [Part::Cut] Cut462
  Base = -> Cut461
  Tool = -> Compound921
FEATURE [Part::Cut] Cut463
  Base = -> Cut462
  Tool = -> Compound922
FEATURE [Part::Cut] Cut464
  Base = -> Cut463
  Tool = -> Compound920
FEATURE [Part::Cylinder] Cylinder1277  label="Válec1277"
  Angle = 360
  AttacherType = Attacher::AttachEngine3D
  Height = 60
  Placement = pos=(41,0,-54) rot=(0,0,1;0rad)
  Radius = 1.5
FEATURE [Part::Cylinder] Cylinder1278  label="Válec1278"
  Angle = 360
  AttacherType = Attacher::AttachEngine3D
  Height = 60
  Placement = pos=(-41,-1.1e-14,-54) rot=(0,0,1;3.14159rad)
  Radius = 1.5
FEATURE [Part::Cylinder] Cylinder1279  label="Válec1279"
  Angle = 360
  AttacherType = Attacher::AttachEngine3D
  Height = 60
  Placement = pos=(-28.9914,-28.9914,-54) rot=(0,0,1;3.92699rad)
  Radius = 1.5
FEATURE [Part::Cylinder] Cylinder1280  label="Válec1280"
  Angle = 360
  AttacherType = Attacher::AttachEngine3D
  Height = 60
  Placement = pos=(28.9914,-28.9914,-54) rot=(0,0,-1;0.785398rad)
  Radius = 1.5
FEATURE [Part::Cylinder] Cylinder1281  label="Válec1281"
  Angle = 360
  AttacherType = Attacher::AttachEngine3D
  Height = 60
  Placement = pos=(28.9914,28.9914,-54) rot=(0,0,1;0.785398rad)
  Radius = 1.5
FEATURE [Part::Cylinder] Cylinder1282  label="Válec1282"
  Angle = 360
  AttacherType = Attacher::AttachEngine3D
  Height = 60
  Placement = pos=(-28.9914,28.9914,-54) rot=(0,0,1;2.35619rad)
  Radius = 1.5
FEATURE [Part::Cylinder] Cylinder1283  label="Válec1283"
  Angle = 360
  AttacherType = Attacher::AttachEngine3D
  Height = 60
  Placement = pos=(1.2e-14,-41,-54) rot=(0,0,-1;1.5708rad)
  Radius = 1.5
FEATURE [Part::Cylinder] Cylinder1284  label="Válec1284"
  Angle = 360
  AttacherType = Attacher::AttachEngine3D
  Height = 60
  Placement = pos=(-4e-15,41,-54) rot=(0,0,1;1.5708rad)
  Radius = 1.5
FEATURE [Part::Compound] Compound923
  Links = -> [Cylinder1281,Cylinder1284,Cylinder1282,Cylinder1278,Cylinder1279,Cylinder1283,Cylinder1280,Cylinder1277]
  Placement = pos=(0,0,0) rot=(0,0,1;0.392699rad)
FEATURE [Part::Cut] Cut465
  Base = -> Cut450
  Tool = -> Compound923
FEATURE [Part::Compound] Compound924  label="J-midi_deep-thin-monoblok"
  Links = -> [Cut465,Cut464,Fillet,Cut449]
FEATURE [Mesh::Feature] Mesh  label="J-midi_deep-thin-monoblok (Meshed)"
FEATURE [Part::Torus] Torus010  label="Anuloid010"
  Angle1 = -180
  Angle2 = 180
  Angle3 = 360
  AttacherType = Attacher::AttachEngine3D
  Placement = pos=(0,0,34) rot=(0,0,1;0rad)
  Radius1 = 46
  Radius2 = 3.1
FEATURE [Part::Cylinder] Cylinder1285  label="Válec1285"
  Angle = 360
  AttacherType = Attacher::AttachEngine3D
  Height = 20
  Placement = pos=(-46.4,0,34) rot=(0,0,1;0rad)
  Radius = 3.5
FEATURE [Part::Cylinder] Cylinder1286  label="Válec1286"
  Angle = 360
  AttacherType = Attacher::AttachEngine3D
  Height = 32
  Placement = pos=(-29.6985,-29.6985,33.5) rot=(0,0,-1;0.785398rad)
  Radius = 1.5
FEATURE [Part::Cylinder] Cylinder1287  label="Válec1287"
  Angle = 360
  AttacherType = Attacher::AttachEngine3D
  Height = 32
  Placement = pos=(-29.6985,29.6985,33.5) rot=(0,0,1;3.92699rad)
  Radius = 1.5
FEATURE [Part::Box] Box544  label="Krychle544"
  AttacherType = Attacher::AttachEngine3D
  Height = 2
  Length = 6
  Placement = pos=(-34.6482,-30.4056,33) rot=(0,0,-1;0.785398rad)
  Width = 8
FEATURE [Part::Box] Box545  label="Krychle545"
  AttacherType = Attacher::AttachEngine3D
  Height = 2
  Length = 6
  Placement = pos=(-3,-46,33) rot=(0,0,1;0rad)
  Width = 8
FEATURE [Part::Box] Box546  label="Krychle546"
  AttacherType = Attacher::AttachEngine3D
  Height = 2
  Length = 6
  Placement = pos=(46,-3,33) rot=(0,0,1;1.5708rad)
  Width = 8
FEATURE [Part::Box] Box547  label="Krychle547"
  AttacherType = Attacher::AttachEngine3D
  Height = 2
  Length = 6
  Placement = pos=(-30.4056,34.6482,33) rot=(0,0,1;3.92699rad)
  Width = 8
FEATURE [Part::Cylinder] Cylinder1288  label="Válec1288"
  Angle = 360
  AttacherType = Attacher::AttachEngine3D
  Height = 32
  Placement = pos=(0,-42,33.5) rot=(0,0,1;0rad)
  Radius = 1.5
FEATURE [Part::Cylinder] Cylinder1289  label="Válec1289"
  Angle = 360
  AttacherType = Attacher::AttachEngine3D
  Height = 32
  Placement = pos=(-1.4e-14,42,33.5) rot=(0,0,1;3.14159rad)
  Radius = 1.5
FEATURE [Part::Box] Box548  label="Krychle548"
  AttacherType = Attacher::AttachEngine3D
  Height = 2
  Length = 6
  Placement = pos=(30.4056,-34.6482,33) rot=(0,0,1;0.785398rad)
  Width = 8
FEATURE [Part::Box] Box549  label="Krychle549"
  AttacherType = Attacher::AttachEngine3D
  Height = 2
  Length = 6
  Placement = pos=(34.6482,30.4056,33) rot=(0,0,1;2.35619rad)
  Width = 8
FEATURE [Part::Cylinder] Cylinder1290  label="Válec1290"
  Angle = 360
  AttacherType = Attacher::AttachEngine3D
  Height = 32
  Placement = pos=(29.6985,-29.6985,33.5) rot=(0,0,1;0.785398rad)
  Radius = 1.5
FEATURE [Part::Cylinder] Cylinder1291  label="Válec1291"
  Angle = 360
  AttacherType = Attacher::AttachEngine3D
  Height = 32
  Placement = pos=(29.6985,29.6985,33.5) rot=(0,0,1;2.35619rad)
  Radius = 1.5
FEATURE [Part::Cylinder] Cylinder1292  label="Válec1292"
  Angle = 360
  AttacherType = Attacher::AttachEngine3D
  Height = 32
  Placement = pos=(-42,-2.4e-14,33.5) rot=(0,0,-1;1.5708rad)
  Radius = 1.5
FEATURE [Part::Cylinder] Cylinder1293  label="Válec1293"
  Angle = 360
  AttacherType = Attacher::AttachEngine3D
  Height = 32
  Placement = pos=(42,6e-15,33.5) rot=(0,0,1;1.5708rad)
  Radius = 1.5
FEATURE [Part::Compound] Compound926
  Links = -> [Cylinder1288,Cylinder1290,Cylinder1293,Cylinder1291,Cylinder1289,Cylinder1287,Cylinder1292,Cylinder1286]
  Placement = pos=(0,0,3) rot=(0,0,1;0.392699rad)
FEATURE [Part::Box] Box550  label="Krychle550"
  AttacherType = Attacher::AttachEngine3D
  Height = 2
  Length = 6
  Placement = pos=(3,46,33) rot=(0,0,1;3.14159rad)
  Width = 8
FEATURE [Part::Box] Box551  label="Krychle551"
  AttacherType = Attacher::AttachEngine3D
  Height = 2
  Length = 6
  Placement = pos=(-46,3,33) rot=(0,0,-1;1.5708rad)
  Width = 8
FEATURE [Part::Compound] Compound925
  Links = -> [Box544,Box548,Box546,Box545,Box549,Box550,Box547,Box551]
  Placement = pos=(0,0,10) rot=(0,0,1;0.392699rad)
FEATURE [Part::FeaturePython] Tube113  # WARN: FeaturePython — macro-defined, semantics opaque (R4)
  AttacherType = Attacher::AttachEngine3D
  Height = 24
  InnerRadius = 40
  OuterRadius = 46
  Placement = pos=(0,0,25) rot=(0,0,1;0rad)
FEATURE [Part::Box] Box552  label="Krychle552"
  AttacherType = Attacher::AttachEngine3D
  Height = 2
  Length = 6
  Placement = pos=(-3,-46,33) rot=(0,0,1;0rad)
  Width = 8
FEATURE [Part::Box] Box553  label="Krychle553"
  AttacherType = Attacher::AttachEngine3D
  Height = 2
  Length = 6
  Placement = pos=(-46,3,33) rot=(0,0,-1;1.5708rad)
  Width = 8
FEATURE [Part::Cylinder] Cylinder1295  label="Válec1295"
  Angle = 360
  AttacherType = Attacher::AttachEngine3D
  Height = 12
  Placement = pos=(-29.6985,-29.6985,33.5) rot=(0,0,-1;0.785398rad)
  Radius = 1.5
FEATURE [Part::Cylinder] Cylinder1296  label="Válec1296"
  Angle = 360
  AttacherType = Attacher::AttachEngine3D
  Height = 12
  Placement = pos=(29.6985,-29.6985,33.5) rot=(0,0,1;0.785398rad)
  Radius = 1.5
FEATURE [Part::Box] Box554  label="Krychle554"
  AttacherType = Attacher::AttachEngine3D
  Height = 2
  Length = 6
  Placement = pos=(30.4056,-34.6482,33) rot=(0,0,1;0.785398rad)
  Width = 8
FEATURE [Part::Box] Box555  label="Krychle555"
  AttacherType = Attacher::AttachEngine3D
  Height = 2
  Length = 6
  Placement = pos=(46,-3,33) rot=(0,0,1;1.5708rad)
  Width = 8
FEATURE [Part::Box] Box556  label="Krychle556"
  AttacherType = Attacher::AttachEngine3D
  Height = 2
  Length = 6
  Placement = pos=(3,46,33) rot=(0,0,1;3.14159rad)
  Width = 8
FEATURE [Part::Cylinder] Cylinder1297  label="Válec1297"
  Angle = 360
  AttacherType = Attacher::AttachEngine3D
  Height = 12
  Placement = pos=(42,6e-15,33.5) rot=(0,0,1;1.5708rad)
  Radius = 1.5
FEATURE [Part::Cylinder] Cylinder1298  label="Válec1298"
  Angle = 360
  AttacherType = Attacher::AttachEngine3D
  Height = 12
  Placement = pos=(0,-42,33.5) rot=(0,0,1;0rad)
  Radius = 1.5
FEATURE [Part::Cylinder] Cylinder1299  label="Válec1299"
  Angle = 360
  AttacherType = Attacher::AttachEngine3D
  Height = 12
  Placement = pos=(-42,-2.4e-14,33.5) rot=(0,0,-1;1.5708rad)
  Radius = 1.5
FEATURE [Part::Cylinder] Cylinder1300  label="Válec1300"
  Angle = 360
  AttacherType = Attacher::AttachEngine3D
  Height = 12
  Placement = pos=(-1.4e-14,42,33.5) rot=(0,0,1;3.14159rad)
  Radius = 1.5
FEATURE [Part::Cylinder] Cylinder1301  label="Válec1301"
  Angle = 360
  AttacherType = Attacher::AttachEngine3D
  Height = 12
  Placement = pos=(29.6985,29.6985,33.5) rot=(0,0,1;2.35619rad)
  Radius = 1.5
FEATURE [Part::Box] Box557  label="Krychle557"
  AttacherType = Attacher::AttachEngine3D
  Height = 2
  Length = 6
  Placement = pos=(34.6482,30.4056,33) rot=(0,0,1;2.35619rad)
  Width = 8
FEATURE [Part::Box] Box558  label="Krychle558"
  AttacherType = Attacher::AttachEngine3D
  Height = 2
  Length = 6
  Placement = pos=(-34.6482,-30.4056,33) rot=(0,0,-1;0.785398rad)
  Width = 8
FEATURE [Part::Cylinder] Cylinder1302  label="Válec1302"
  Angle = 360
  AttacherType = Attacher::AttachEngine3D
  Height = 12
  Placement = pos=(-29.6985,29.6985,33.5) rot=(0,0,1;3.92699rad)
  Radius = 1.5
FEATURE [Part::Compound] Compound928
  Links = -> [Cylinder1298,Cylinder1296,Cylinder1297,Cylinder1301,Cylinder1300,Cylinder1302,Cylinder1299,Cylinder1295]
  Placement = pos=(0,0,4) rot=(0,0,1;0.392699rad)
FEATURE [Part::Box] Box559  label="Krychle559"
  AttacherType = Attacher::AttachEngine3D
  Height = 2
  Length = 6
  Placement = pos=(-30.4056,34.6482,33) rot=(0,0,1;3.92699rad)
  Width = 8
FEATURE [Part::Compound] Compound927
  Links = -> [Box558,Box554,Box555,Box552,Box557,Box556,Box559,Box553]
  Placement = pos=(0,0,7) rot=(0,0,1;0.392699rad)
FEATURE [Part::FeaturePython] Tube114  # WARN: FeaturePython — macro-defined, semantics opaque (R4)
  AttacherType = Attacher::AttachEngine3D
  Height = 1
  InnerRadius = 36
  OuterRadius = 46
  Placement = pos=(0,0,45) rot=(0,0,1;0rad)
FEATURE [Part::FeaturePython] Tube115  label="ZKL-61816-5"  # WARN: FeaturePython — macro-defined, semantics opaque (R4)
  AttacherType = Attacher::AttachEngine3D
  Height = 12
  InnerRadius = 40
  OuterRadius = 50
  Placement = pos=(0,0,24) rot=(0,0,1;0rad)
FEATURE [Part::Cut] Cut469  label="J-midi_deep-thin-actuator-washer"
  Base = -> Tube114
  Placement = pos=(0,0,4) rot=(0,0,1;0rad)
  Tool = -> Compound928
FEATURE [Part::Box] Box560  label="Krychle560"
  AttacherType = Attacher::AttachEngine3D
  Height = 2
  Length = 6
  Placement = pos=(3,46,33) rot=(0,0,1;3.14159rad)
  Width = 8
FEATURE [Part::Box] Box561  label="Krychle561"
  AttacherType = Attacher::AttachEngine3D
  Height = 2
  Length = 6
  Placement = pos=(30.4056,-34.6482,33) rot=(0,0,1;0.785398rad)
  Width = 8
FEATURE [Part::Cylinder] Cylinder1303  label="Válec1303"
  Angle = 360
  AttacherType = Attacher::AttachEngine3D
  Height = 12
  Radius = 40
FEATURE [Part::Box] Box562  label="Krychle562"
  AttacherType = Attacher::AttachEngine3D
  Height = 2
  Length = 6
  Placement = pos=(-34.6482,-30.4056,33) rot=(0,0,-1;0.785398rad)
  Width = 8
FEATURE [Part::Box] Box563  label="Krychle563"
  AttacherType = Attacher::AttachEngine3D
  Height = 2
  Length = 6
  Placement = pos=(34.6482,30.4056,33) rot=(0,0,1;2.35619rad)
  Width = 8
FEATURE [Part::Box] Box564  label="Krychle564"
  AttacherType = Attacher::AttachEngine3D
  Height = 2
  Length = 6
  Placement = pos=(-3,-46,33) rot=(0,0,1;0rad)
  Width = 8
FEATURE [Part::Box] Box565  label="Krychle565"
  AttacherType = Attacher::AttachEngine3D
  Height = 2
  Length = 6
  Placement = pos=(-30.4056,34.6482,33) rot=(0,0,1;3.92699rad)
  Width = 8
FEATURE [Part::Cylinder] Cylinder1304  label="Válec1304"
  Angle = 360
  AttacherType = Attacher::AttachEngine3D
  Height = 12
  Radius = 40
FEATURE [Part::Box] Box566  label="Krychle566"
  AttacherType = Attacher::AttachEngine3D
  Height = 2
  Length = 6
  Placement = pos=(-46,3,33) rot=(0,0,-1;1.5708rad)
  Width = 8
FEATURE [Part::Box] Box567  label="Krychle567"
  AttacherType = Attacher::AttachEngine3D
  Height = 2
  Length = 6
  Placement = pos=(46,-3,33) rot=(0,0,1;1.5708rad)
  Width = 8
FEATURE [Part::Compound] Compound929
  Links = -> [Box562,Box561,Box567,Box564,Box563,Box560,Box565,Box566]
  Placement = pos=(0,0,7) rot=(0,0,1;0.392699rad)
FEATURE [Part::FeaturePython] wormgear069  # WARN: FeaturePython — macro-defined, semantics opaque (R4)
  AttacherType = Attacher::AttachEngine3D
  Placement = pos=(0,0,0) rot=(0,0,1;0.10472rad)
  beta = 38.7636
  clearance = 0.25
  diameter = 67.25
  head = 0
  height = 14
  module = 1.5
  pressure_angle = 20
  reverse_pitch = true
  teeth = 36
  version = 0.0.3
FEATURE [Part::Cut] Cut471
  Base = -> Cylinder1304
  Placement = pos=(0,0,33) rot=(0,0,1;0.466876rad)
  Tool = -> wormgear069
FEATURE [Part::Cut] Cut472
  Base = -> Cut471
  Tool = -> Compound929
FEATURE [Part::FeaturePython] wormgear070  # WARN: FeaturePython — macro-defined, semantics opaque (R4)
  AttacherType = Attacher::AttachEngine3D
  Placement = pos=(0,0,0) rot=(0,0,-1;0.1309rad)
  beta = 38.7636
  clearance = 0.25
  diameter = 67.25
  head = 0
  height = 14
  module = 1.5
  pressure_angle = 20
  reverse_pitch = false
  teeth = 36
  version = 0.0.3
FEATURE [Part::Cut] Cut470
  Base = -> Cylinder1303
  Placement = pos=(0,0,21) rot=(0,0,1;0.258309rad)
  Tool = -> wormgear070
FEATURE [Part::Compound] Compound930
  Links = -> [Cut472,Cut470]
  Placement = pos=(0,0,4) rot=(0,0,1;0rad)
FEATURE [Part::Cut] Cut473
  Base = -> Tube113
  Tool = -> Tube115
FEATURE [Part::FeaturePython] Tube116  label="ZKL-61816-6"  # WARN: FeaturePython — macro-defined, semantics opaque (R4)
  AttacherType = Attacher::AttachEngine3D
  Height = 11
  InnerRadius = 40
  OuterRadius = 50
  Placement = pos=(0,0,24) rot=(0,0,1;0rad)
FEATURE [Part::Cut] Cut474
  Base = -> Compound930
  Tool = -> Tube116
FEATURE [Part::Cut] Cut475
  Base = -> Cut473
  Tool = -> Compound926
FEATURE [Part::Cut] Cut476
  Base = -> Cut475
  Tool = -> Compound925
FEATURE [Part::Box] Box372  label="Krychle372"
  AttacherType = Attacher::AttachEngine3D
  Height = 60
  Length = 50
  Placement = pos=(0,0,8) rot=(0,0,1;1.36136rad)
  Width = 50
FEATURE [Part::Cylinder] Cylinder1045  label="Válec1045"
  Angle = 360
  AttacherType = Attacher::AttachEngine3D
  Height = 3
  Placement = pos=(26,4,-6) rot=(0,0,1;0rad)
  Radius = 3
FEATURE [Part::Cylinder] Cylinder1046  label="Válec1046"
  Angle = 360
  AttacherType = Attacher::AttachEngine3D
  Height = 8
  Radius = 36
FEATURE [Part::Cylinder] Cylinder1047  label="Válec1047"
  Angle = 360
  AttacherType = Attacher::AttachEngine3D
  Height = 80
  Placement = pos=(26,-4,-6) rot=(0,0,1;0rad)
  Radius = 1.45
FEATURE [Part::Cylinder] Cylinder1048  label="Válec1048"
  Angle = 360
  AttacherType = Attacher::AttachEngine3D
  Height = 6
  Placement = pos=(11,19.0526,2) rot=(0,0,1;4.18879rad)
  Radius = 8
FEATURE [Part::Box] Box373  label="Krychle373"
  AttacherType = Attacher::AttachEngine3D
  Height = 60
  Length = 50
  Placement = pos=(0,0,8) rot=(0,0,1;2.61799rad)
  Width = 100
FEATURE [Part::Cylinder] Cylinder1049  label="Válec1049"
  Angle = 360
  AttacherType = Attacher::AttachEngine3D
  Height = 6
  Placement = pos=(11,-19.0526,2) rot=(0,0,1;2.0944rad)
  Radius = 8
FEATURE [Part::Cylinder] Cylinder1050  label="Válec1050"
  Angle = 360
  AttacherType = Attacher::AttachEngine3D
  Height = 20
  Placement = pos=(0,0,-4) rot=(0,0,1;0rad)
  Radius = 12
FEATURE [Part::Cut] Cut381
  Base = -> Cylinder1046
  Tool = -> Cylinder1050
FEATURE [Part::Cylinder] Cylinder1051  label="Válec1051"
  Angle = 360
  AttacherType = Attacher::AttachEngine3D
  Height = 80
  Placement = pos=(26,4,-6) rot=(0,0,1;0rad)
  Radius = 1.45
FEATURE [Part::Compound] Compound839
  Links = -> [Cylinder1051,Cylinder1047]
  Placement = pos=(0,0,0) rot=(0,0,1;1.0472rad)
FEATURE [Part::Box] Box374  label="Krychle374"
  AttacherType = Attacher::AttachEngine3D
  Height = 60
  Length = 50
  Placement = pos=(0,0,8) rot=(0,0,-1;0.837758rad)
  Width = 50
FEATURE [Part::Cylinder] Cylinder1052  label="Válec1052"
  Angle = 360
  AttacherType = Attacher::AttachEngine3D
  Height = 3
  Placement = pos=(26,-4,-6) rot=(0,0,1;0rad)
  Radius = 3
FEATURE [Part::Compound] Compound840
  Links = -> [Cylinder1045,Cylinder1052]
  Placement = pos=(0,0,6) rot=(0,0,1;2.0944rad)
FEATURE [Part::Cylinder] Cylinder1053  label="Válec1053"
  Angle = 360
  AttacherType = Attacher::AttachEngine3D
  Height = 60
  Placement = pos=(26,4,-6) rot=(0,0,1;0rad)
  Radius = 1.45
FEATURE [Part::Cylinder] Cylinder1054  label="Válec1054"
  Angle = 360
  AttacherType = Attacher::AttachEngine3D
  Height = 6
  Placement = pos=(-22,0,2) rot=(0,0,1;0rad)
  Radius = 8
FEATURE [Part::Cylinder] Cylinder1055  label="Válec1055"
  Angle = 360
  AttacherType = Attacher::AttachEngine3D
  Height = 60
  Placement = pos=(26,-4,-6) rot=(0,0,1;0rad)
  Radius = 1.45
FEATURE [Part::Compound] Compound837
  Links = -> [Cylinder1053,Cylinder1055]
  Placement = pos=(0,0,0) rot=(0,0,1;4.18879rad)
FEATURE [Part::Box] Box375  label="Krychle375"
  AttacherType = Attacher::AttachEngine3D
  Height = 60
  Length = 50
  Placement = pos=(0,0,8) rot=(0,0,1;4.18879rad)
  Width = 100
FEATURE [Part::FeaturePython] Tube088  # WARN: FeaturePython — macro-defined, semantics opaque (R4)
  AttacherType = Attacher::AttachEngine3D
  Height = 1
  InnerRadius = 7
  OuterRadius = 8
  Placement = pos=(-22,0,2) rot=(0,0,1;0rad)
FEATURE [Part::FeaturePython] Tube089  # WARN: FeaturePython — macro-defined, semantics opaque (R4)
  AttacherType = Attacher::AttachEngine3D
  Height = 51
  InnerRadius = 15
  OuterRadius = 30
  Placement = pos=(0,0,8) rot=(0,0,1;0rad)
FEATURE [Part::FeaturePython] Tube090  # WARN: FeaturePython — macro-defined, semantics opaque (R4)
  AttacherType = Attacher::AttachEngine3D
  Height = 1
  InnerRadius = 7
  OuterRadius = 8
  Placement = pos=(11,-19.0526,2) rot=(0,0,1;2.0944rad)
FEATURE [Part::FeaturePython] Tube091  # WARN: FeaturePython — macro-defined, semantics opaque (R4)
  AttacherType = Attacher::AttachEngine3D
  Height = 1
  InnerRadius = 12
  OuterRadius = 20
  Placement = pos=(0,0,-1) rot=(0,0,1;0rad)
FEATURE [Part::FeaturePython] Tube092  # WARN: FeaturePython — macro-defined, semantics opaque (R4)
  AttacherType = Attacher::AttachEngine3D
  Height = 1
  InnerRadius = 7
  OuterRadius = 8
  Placement = pos=(11,19.0526,2) rot=(0,0,1;4.18879rad)
FEATURE [Part::FeaturePython] Tube093  # WARN: FeaturePython — macro-defined, semantics opaque (R4)
  AttacherType = Attacher::AttachEngine3D
  Height = 8
  InnerRadius = 12
  OuterRadius = 15
  Placement = pos=(0,0,-9) rot=(0,0,1;0rad)
FEATURE [Part::Compound] Compound841
  Links = -> [Cylinder1054,Cylinder1049,Cylinder1048]
FEATURE [Part::Compound] Compound842
  Links = -> [Cylinder1053,Cylinder1055]
FEATURE [Part::Compound] Compound843
  Links = -> [Cylinder1045,Cylinder1052]
  Placement = pos=(0,0,6) rot=(0,0,1;0rad)
FEATURE [Part::Compound] Compound844
  Links = -> [Cylinder1045,Cylinder1052]
  Placement = pos=(0,0,6) rot=(0,0,1;4.18879rad)
FEATURE [Part::Compound] Compound836
  Links = -> [Compound840,Compound844,Compound843]
FEATURE [Part::Compound] Compound847
  Links = -> [Tube090,Tube092,Tube088]
FEATURE [Part::Compound] Compound848
  Links = -> [Cylinder1053,Cylinder1055]
  Placement = pos=(0,0,0) rot=(0,0,1;2.0944rad)
FEATURE [Part::Compound] Compound845
  Links = -> [Compound848,Compound837,Compound842]
FEATURE [Part::Cut] Cut390
  Base = -> Cut381
  Tool = -> Compound841
FEATURE [Part::Cut] Cut385
  Base = -> Cut390
  Tool = -> Compound836
FEATURE [Part::Cut] Cut387
  Base = -> Cut385
  Tool = -> Compound845
FEATURE [Part::Cut] Cut391
  Base = -> Tube089
  Tool = -> Box375
FEATURE [Part::Cut] Cut388
  Base = -> Cut391
  Tool = -> Box373
FEATURE [Part::Cut] Cut389
  Base = -> Cut388
  Tool = -> Box374
FEATURE [Part::Cut] Cut384
  Base = -> Cut389
  Tool = -> Box372
FEATURE [Part::Cut] Cut382
  Base = -> Cut384
  Placement = pos=(0,0,0) rot=(0,0,1;3.14159rad)
  Tool = -> Compound839
FEATURE [Part::Cut] Cut383
  Base = -> Cut384
  Placement = pos=(0,0,0) rot=(0,0,-1;1.0472rad)
  Tool = -> Compound839
FEATURE [Part::Cut] Cut386
  Base = -> Cut384
  Placement = pos=(0,0,0) rot=(0,0,1;1.0472rad)
  Tool = -> Compound839
FEATURE [Part::Compound] Compound835
  Links = -> [Cut383,Cut382,Cut386]
FEATURE [Part::Compound] Compound846  label="J-midi_pikovina002"
  Links = -> [Compound835,Cut387,Compound847]
FEATURE [Part::Compound] Compound838  label="auxi1"
  Links = -> [Tube093,Tube091,Compound846]
FEATURE [Part::Chamfer] Chamfer027  label="auxi2"
  Base = -> Compound838
  Edges = 1 edges r=1: [Edge3]
  Placement = pos=(0,0,100) rot=(0,0,1;0rad)
FEATURE [Part::Chamfer] Chamfer028  label="J-midi-deep_pikovina_fixo"
  Base = -> Chamfer027
  Edges = 1 edges r=2: [Edge71]
FEATURE [Part::Cylinder] Cylinder632  label="Válec632"
  Angle = 360
  AttacherType = Attacher::AttachEngine3D
  Height = 6
  Placement = pos=(11,19.0526,2) rot=(0,0,1;4.18879rad)
  Radius = 8
FEATURE [Part::Cylinder] Cylinder633  label="Válec633"
  Angle = 360
  AttacherType = Attacher::AttachEngine3D
  Height = 6
  Placement = pos=(-22,0,2) rot=(0,0,1;0rad)
  Radius = 8
FEATURE [Part::Cylinder] Cylinder634  label="Válec634"
  Angle = 360
  AttacherType = Attacher::AttachEngine3D
  Height = 6
  Placement = pos=(11,-19.0526,2) rot=(0,0,1;2.0944rad)
  Radius = 8
FEATURE [Part::Cylinder] Cylinder635  label="Válec635"
  Angle = 360
  AttacherType = Attacher::AttachEngine3D
  Height = 8
  Radius = 36
FEATURE [Part::Cylinder] Cylinder636  label="Válec636"
  Angle = 360
  AttacherType = Attacher::AttachEngine3D
  Height = 6
  Placement = pos=(0,0,2) rot=(0,0,1;0rad)
  Radius = 8
FEATURE [Part::Cylinder] Cylinder637  label="Válec637"
  Angle = 360
  AttacherType = Attacher::AttachEngine3D
  Height = 3
  Placement = pos=(26,-4,-6) rot=(0,0,1;0rad)
  Radius = 3
FEATURE [Part::Cylinder] Cylinder638  label="Válec638"
  Angle = 360
  AttacherType = Attacher::AttachEngine3D
  Height = 60
  Placement = pos=(26,4,-6) rot=(0,0,1;0rad)
  Radius = 1.5
FEATURE [Part::Cylinder] Cylinder639  label="Válec639"
  Angle = 360
  AttacherType = Attacher::AttachEngine3D
  Height = 60
  Placement = pos=(26,-4,-6) rot=(0,0,1;0rad)
  Radius = 1.5
FEATURE [Part::Compound] Compound657
  Links = -> [Cylinder638,Cylinder639]
  Placement = pos=(0,0,0) rot=(0,0,1;2.0944rad)
FEATURE [Part::Cylinder] Cylinder640  label="Válec640"
  Angle = 360
  AttacherType = Attacher::AttachEngine3D
  Height = 3
  Placement = pos=(26,4,-6) rot=(0,0,1;0rad)
  Radius = 3
FEATURE [Part::Cylinder] Cylinder641  label="Válec641"
  Angle = 360
  AttacherType = Attacher::AttachEngine3D
  Height = 1
  Placement = pos=(0,0,-1) rot=(0,0,1;0rad)
  Radius = 10
FEATURE [Part::Cylinder] Cylinder642  label="Válec642"
  Angle = 360
  AttacherType = Attacher::AttachEngine3D
  Height = 8
  Placement = pos=(0,0,-9) rot=(0,0,1;0rad)
  Radius = 7.5
FEATURE [Part::FeaturePython] Tube045  # WARN: FeaturePython — macro-defined, semantics opaque (R4)
  AttacherType = Attacher::AttachEngine3D
  Height = 1
  InnerRadius = 7
  OuterRadius = 8
  Placement = pos=(-22,0,2) rot=(0,0,1;0rad)
FEATURE [Part::FeaturePython] Tube046  # WARN: FeaturePython — macro-defined, semantics opaque (R4)
  AttacherType = Attacher::AttachEngine3D
  Height = 1
  InnerRadius = 7
  OuterRadius = 8
  Placement = pos=(11,-19.0526,2) rot=(0,0,1;2.0944rad)
FEATURE [Part::FeaturePython] Tube047  # WARN: FeaturePython — macro-defined, semantics opaque (R4)
  AttacherType = Attacher::AttachEngine3D
  Height = 1
  InnerRadius = 7
  OuterRadius = 8
  Placement = pos=(0,0,2) rot=(0,0,1;4.18879rad)
FEATURE [Part::FeaturePython] Tube048  # WARN: FeaturePython — macro-defined, semantics opaque (R4)
  AttacherType = Attacher::AttachEngine3D
  Height = 1
  InnerRadius = 7
  OuterRadius = 8
  Placement = pos=(11,19.0526,2) rot=(0,0,1;4.18879rad)
FEATURE [Part::Compound] Compound658
  Links = -> [Cylinder640,Cylinder637]
  Placement = pos=(0,0,6) rot=(0,0,1;2.0944rad)
FEATURE [Part::Compound] Compound659
  Links = -> [Cylinder638,Cylinder639]
  Placement = pos=(0,0,0) rot=(0,0,1;4.18879rad)
FEATURE [Part::Compound] Compound660
  Links = -> [Cylinder638,Cylinder639]
FEATURE [Part::Compound] Compound661
  Links = -> [Compound657,Compound659,Compound660]
FEATURE [Part::Compound] Compound663
  Links = -> [Cylinder640,Cylinder637]
  Placement = pos=(0,0,6) rot=(0,0,1;0rad)
FEATURE [Part::Compound] Compound665
  Links = -> [Cylinder640,Cylinder637]
  Placement = pos=(0,0,6) rot=(0,0,1;4.18879rad)
FEATURE [Part::Compound] Compound664
  Links = -> [Compound658,Compound665,Compound663]
FEATURE [Part::Compound] Compound666
  Links = -> [Cylinder633,Cylinder634,Cylinder632,Cylinder636]
FEATURE [Part::Cut] Cut287
  Base = -> Cylinder635
  Tool = -> Compound666
FEATURE [Part::Cut] Cut286
  Base = -> Cut287
  Tool = -> Compound661
FEATURE [Part::Cut] Cut285
  Base = -> Cut286
  Tool = -> Compound664
FEATURE [Part::Compound] Compound662  label="J-midi_quikovina_fixo2"
  Links = -> [Tube045,Tube047,Tube046,Tube048,Cut285]
FEATURE [Part::Chamfer] Chamfer029
  Base = -> Cylinder642
  Edges = 1 edges r=1: [Edge3]
FEATURE [Part::Compound] Compound667  label="auxi3"
  Links = -> [Chamfer029,Cylinder641,Compound662]
  Placement = pos=(0,0,-32) rot=(0,0,1;0rad)
FEATURE [Part::Chamfer] Chamfer036  label="J-midi-deep_quikovina_fixo"
  Base = -> Compound667
  Edges = 1 edges r=2: [Edge35]
FEATURE [Part::FeaturePython] Tube117  label="ZKL-61816-subwasher"  # WARN: FeaturePython — macro-defined, semantics opaque (R4)
  AttacherType = Attacher::AttachEngine3D
  Height = 0.8
  InnerRadius = 40
  OuterRadius = 42
  Placement = pos=(0,0,35.2) rot=(0,0,1;0rad)
FEATURE [Mesh::Feature] Mesh001  label="J-midi-deep_pikovina_fixo (Meshed)"
FEATURE [Part::Wedge] Wedge038  label="Klín038"
  AttacherType = Attacher::AttachEngine3D
  Placement = pos=(0,0,12) rot=(0,0,1;0rad)
  X2max = 0
  X2min = 0
  Xmax = 10
  Xmin = -10
  Ymax = 0
  Ymin = -32
  Z2max = 12
  Z2min = 0
  Zmax = 12
  Zmin = 0
FEATURE [Part::Wedge] Wedge039  label="Klín039"
  AttacherType = Attacher::AttachEngine3D
  Placement = pos=(0,0,12) rot=(0,0,1;3.14159rad)
  X2max = 0
  X2min = 0
  Xmax = 10
  Xmin = -10
  Ymax = 0
  Ymin = -32
  Z2max = 12
  Z2min = 0
  Zmax = 12
  Zmin = 0
FEATURE [Part::Cylinder] Cylinder1305  label="Válec1305"
  Angle = 360
  AttacherType = Attacher::AttachEngine3D
  Height = 20
  Placement = pos=(4,4,-88) rot=(0,0,1;3.14159rad)
  Radius = 1
FEATURE [Part::Cylinder] Cylinder1306  label="Válec1306"
  Angle = 360
  AttacherType = Attacher::AttachEngine3D
  Height = 4
  Placement = pos=(0,0,15) rot=(0,0,1;0rad)
  Radius = 7.5
FEATURE [Part::Cylinder] Cylinder1307  label="Válec1307"
  Angle = 360
  AttacherType = Attacher::AttachEngine3D
  Height = 20
  Placement = pos=(-4,4,-88) rot=(0,0,-1;1.5708rad)
  Radius = 1
FEATURE [Part::Cylinder] Cylinder1308  label="Válec1308"
  Angle = 360
  AttacherType = Attacher::AttachEngine3D
  Height = 20
  Placement = pos=(4,-4,-88) rot=(0,0,1;1.5708rad)
  Radius = 1
FEATURE [Part::Cylinder] Cylinder1309  label="Válec1309"
  Angle = 360
  AttacherType = Attacher::AttachEngine3D
  Height = 20
  Placement = pos=(-4,4,-88) rot=(0,0,-1;1.5708rad)
  Radius = 1
FEATURE [Part::Cylinder] Cylinder1310  label="Válec1310"
  Angle = 360
  AttacherType = Attacher::AttachEngine3D
  Height = 2
  Placement = pos=(-4,-4,-88) rot=(0,0,1;0rad)
  Radius = 2
FEATURE [Part::Cylinder] Cylinder1311  label="Válec1311"
  Angle = 360
  AttacherType = Attacher::AttachEngine3D
  Height = 20
  Placement = pos=(-4,-4,-88) rot=(0,0,1;0rad)
  Radius = 1
FEATURE [Part::Cylinder] Cylinder1312  label="Válec1312"
  Angle = 360
  AttacherType = Attacher::AttachEngine3D
  Height = 2
  Placement = pos=(-4,4,-88) rot=(0,0,-1;1.5708rad)
  Radius = 2
FEATURE [Part::Cylinder] Cylinder1313  label="Válec1313"
  Angle = 360
  AttacherType = Attacher::AttachEngine3D
  Height = 2
  Placement = pos=(4,4,-88) rot=(0,0,1;3.14159rad)
  Radius = 2
FEATURE [Part::Cylinder] Cylinder1314  label="Válec1314"
  Angle = 360
  AttacherType = Attacher::AttachEngine3D
  Height = 20
  Placement = pos=(4,-4,-88) rot=(0,0,1;1.5708rad)
  Radius = 1
FEATURE [Part::Cylinder] Cylinder1315  label="Válec1315"
  Angle = 360
  AttacherType = Attacher::AttachEngine3D
  Height = 20
  Placement = pos=(4,-4,-88) rot=(0,0,1;1.5708rad)
  Radius = 1
FEATURE [Part::Cylinder] Cylinder1316  label="Válec1316"
  Angle = 360
  AttacherType = Attacher::AttachEngine3D
  Height = 2
  Placement = pos=(4,-4,-88) rot=(0,0,1;1.5708rad)
  Radius = 2
FEATURE [Part::FeaturePython] Tube118  # WARN: FeaturePython — macro-defined, semantics opaque (R4)
  AttacherType = Attacher::AttachEngine3D
  Height = 10
  InnerRadius = 2.75
  OuterRadius = 7.5
  Placement = pos=(0,0,19) rot=(0,0,1;0rad)
FEATURE [Part::FeaturePython] wormgear071  # WARN: FeaturePython — macro-defined, semantics opaque (R4)
  AttacherType = Attacher::AttachEngine3D
  Placement = pos=(0,0,29) rot=(0,0,1;0.994838rad)
  beta = 40.6013
  clearance = 0.25
  diameter = 21
  head = 0.25
  height = 12
  module = 1.5
  pressure_angle = 20
  reverse_pitch = false
  teeth = 12
  version = 0.0.3
FEATURE [Part::FeaturePython] Tube119  # WARN: FeaturePython — macro-defined, semantics opaque (R4)
  AttacherType = Attacher::AttachEngine3D
  Height = 12
  InnerRadius = 3.75
  OuterRadius = 7.5
  Placement = pos=(0,0,12) rot=(0,0,1;0rad)
FEATURE [Part::Cylinder] Cylinder1317  label="Válec1317"
  Angle = 360
  AttacherType = Attacher::AttachEngine3D
  Height = 20
  Placement = pos=(4,4,-88) rot=(0,0,1;3.14159rad)
  Radius = 1
FEATURE [Part::Cylinder] Cylinder1318  label="Válec1318"
  Angle = 360
  AttacherType = Attacher::AttachEngine3D
  Height = 20
  Placement = pos=(-4,4,-88) rot=(0,0,-1;1.5708rad)
  Radius = 1
FEATURE [Part::Compound] Compound933
  Links = -> [Cylinder1311,Cylinder1315,Cylinder1317,Cylinder1318]
  Placement = pos=(0,0,91) rot=(0,0,1;0rad)
FEATURE [Part::Cut] Cut477
  Base = -> Tube118
  Tool = -> Compound933
FEATURE [Part::Cylinder] Cylinder1319  label="Válec1319"
  Angle = 360
  AttacherType = Attacher::AttachEngine3D
  Height = 20
  Placement = pos=(4,4,-88) rot=(0,0,1;3.14159rad)
  Radius = 1
FEATURE [Part::Cylinder] Cylinder1320  label="Válec1320"
  Angle = 360
  AttacherType = Attacher::AttachEngine3D
  Height = 20
  Placement = pos=(-4,-4,-88) rot=(0,0,1;0rad)
  Radius = 1
FEATURE [Part::Compound] Compound932
  Links = -> [Cylinder1320,Cylinder1308,Cylinder1305,Cylinder1307]
  Placement = pos=(0,0,91) rot=(0,0,1;0rad)
FEATURE [Part::Cylinder] Cylinder1321  label="Válec1321"
  Angle = 360
  AttacherType = Attacher::AttachEngine3D
  Height = 20
  Placement = pos=(-4,-4,-88) rot=(0,0,1;0rad)
  Radius = 1
FEATURE [Part::Cylinder] Cylinder1322  label="Válec1322"
  Angle = 360
  AttacherType = Attacher::AttachEngine3D
  Height = 60
  Placement = pos=(0,0,-10) rot=(0,0,1;0rad)
  Radius = 2.75
FEATURE [Part::Compound] Compound936
  Links = -> [Cylinder1310,Cylinder1316,Cylinder1313,Cylinder1312]
  Placement = pos=(0,0,91) rot=(0,0,1;0rad)
FEATURE [Part::Compound] Compound937
  Links = -> [Cylinder1321,Cylinder1314,Cylinder1319,Cylinder1309]
  Placement = pos=(0,0,91) rot=(0,0,1;0rad)
FEATURE [Part::Cut] Cut478
  Base = -> Cylinder1306
  Tool = -> Compound937
FEATURE [Part::Cut] Cut479
  Base = -> wormgear071
  Tool = -> Cylinder1322
FEATURE [Part::Wedge] Wedge036  label="Klín036"
  AttacherType = Attacher::AttachEngine3D
  Placement = pos=(0,0,12) rot=(0,0,1;1.5708rad)
  X2max = 0
  X2min = 0
  Xmax = 10
  Xmin = -10
  Ymax = 0
  Ymin = -32
  Z2max = 12
  Z2min = 0
  Zmax = 12
  Zmin = 0
FEATURE [Part::Wedge] Wedge037  label="Klín037"
  AttacherType = Attacher::AttachEngine3D
  Placement = pos=(0,0,12) rot=(0,0,-1;1.5708rad)
  X2max = 0
  X2min = 0
  Xmax = 10
  Xmin = -10
  Ymax = 0
  Ymin = -32
  Z2max = 12
  Z2min = 0
  Zmax = 12
  Zmin = 0
FEATURE [Part::Compound] Compound935
  Links = -> [Wedge038,Wedge036,Wedge039,Wedge037]
FEATURE [Part::Cut] Cut482
  Base = -> Tube119
  Placement = pos=(0,0,-9) rot=(0,0,1;0rad)
  Tool = -> Compound935
FEATURE [Part::Chamfer] Chamfer031
  Base = -> Cut482
  Edges = 8 edges r=1: [Edge7,Edge8,Edge21,Edge22,Edge31,Edge32,Edge45,Edge46]
FEATURE [Part::Cut] Cut481
  Base = -> Chamfer031
  Tool = -> Compound936
FEATURE [Part::Cut] Cut480
  Base = -> Cut481
  Tool = -> Compound932
FEATURE [Part::Compound] Compound934  label="J-midi_inner-planeo-m1.5-reinforced_v5.0"
  Links = -> [Cut479,Cut480,Cut478,Cut477]
  Placement = pos=(0,0,8) rot=(0,0,1;0.10472rad)
FEATURE [Mesh::Feature] Mesh002  label="J-midi_inner-planeo-m1.5-reinforced_v5.0 (Meshed)"
FEATURE [Part::Chamfer] Chamfer037
  Base = -> Cut474
  Edges = 1 edges r=1: [Edge540]
FEATURE [Part::Compound] Compound938  label="J-midi-deep-thin_actuator-ring-m1.5"
  Links = -> [Cut476,Tube117,Chamfer037]
FEATURE [Part::FeaturePython] Tube125  label="ZKL-6816-separator"  # WARN: FeaturePython — macro-defined, semantics opaque (R4)
  AttacherType = Attacher::AttachEngine3D
  Height = 0.8
  InnerRadius = 44.9
  OuterRadius = 49.9
  Placement = pos=(0,0,15) rot=(0,0,1;0rad)
